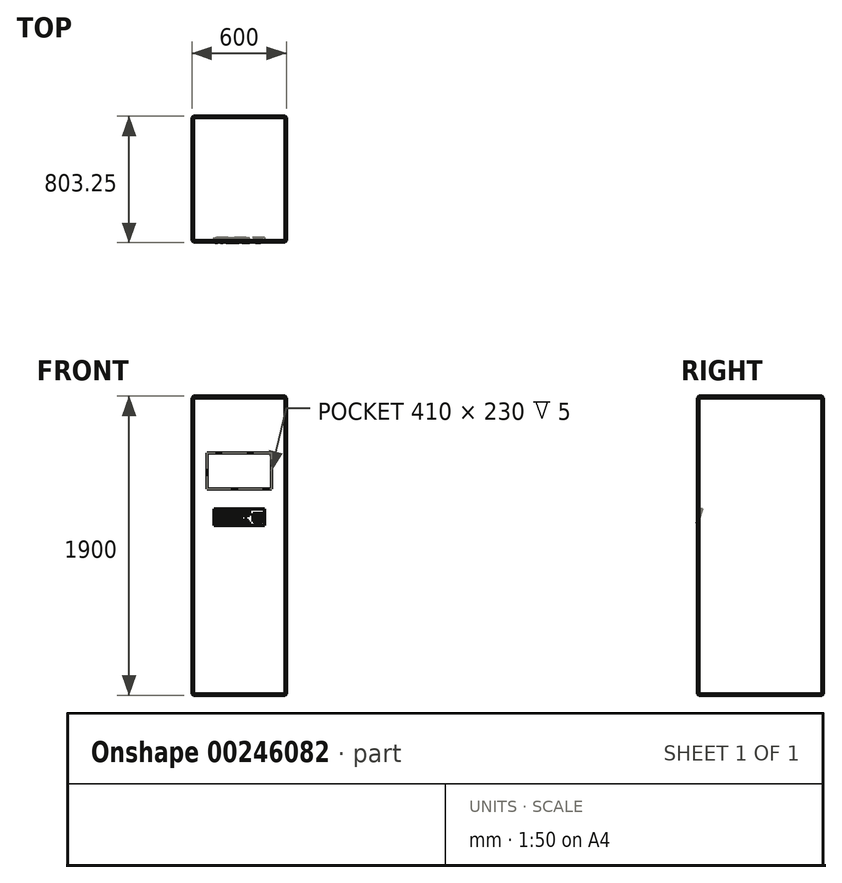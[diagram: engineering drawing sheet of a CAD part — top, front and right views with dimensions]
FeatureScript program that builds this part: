
annotation { "Feature Type Name" : "Feature", "Feature Type Description" : "" }
export const myFeature = defineFeature(function(context is Context, id is Id, definition is map)
    precondition{}
    {
        {
            var Q0;
            Q0=qCreatedBy(makeId("Top.planeOp"),FACE);
            var sketch = newSketch(context, id + "F0", { "sketchPlane" : qUnion([Q0])});
            skLineSegment(sketch, "E0.bottom", {"start": v(-300, 400) * mm, "end": v(300, 400) * mm});
            skLineSegment(sketch, "E0.top", {"start": v(-300, -400) * mm, "end": v(300, -400) * mm});
            skLineSegment(sketch, "E0.left", {"start": v(-300, 400) * mm, "end": v(-300, -400) * mm});
            skLineSegment(sketch, "E0.right", {"start": v(300, 400) * mm, "end": v(300, -400) * mm});
            skSolve(sketch);
        }
        {
            var Q0;
            Q0=makeQuery(id+"F0.imprint","IMPRINT",FACE,{"disambiguationData":[TD([[makeQuery(id+"F0.imprint","IMPRINT",EDGE,{"derivedFrom":sQuery(id+"F0.wireOp",EDGE,"E0.bottom")}),-1.0]])]});
            extrude(context, id + "F1", {"entities" : qUnion([Q0]), "depth" : 1900 * mm});
        }
        {
            var Q0;
            Q0=makeQuery(id+"F1.opExtrude","CAP_EDGE",EDGE,{"disambiguationData":[OSD([sQuery(id+"F0.wireOp",EDGE,"E0.top")])],"isStart":false});
            var Q1;
            Q1=makeQuery(id+"F1.opExtrude","SWEPT_EDGE",EDGE,{"disambiguationData":[OSD([sQuery(id+"F0.wireOp",EDGE,"E0.top"),sQuery(id+"F0.wireOp",EDGE,"E0.right")])]});
            var Q2;
            Q2=makeQuery(id+"F1.opExtrude","SWEPT_EDGE",EDGE,{"disambiguationData":[OSD([sQuery(id+"F0.wireOp",EDGE,"E0.top"),sQuery(id+"F0.wireOp",EDGE,"E0.left")])]});
            var Q3;
            Q3=makeQuery(id+"F1.opExtrude","CAP_EDGE",EDGE,{"disambiguationData":[OSD([sQuery(id+"F0.wireOp",EDGE,"E0.top")])],"isStart":true});
            var Q4;
            Q4=makeQuery(id+"F1.opExtrude","CAP_EDGE",EDGE,{"disambiguationData":[OSD([sQuery(id+"F0.wireOp",EDGE,"E0.right")])],"isStart":true});
            var Q5;
            Q5=makeQuery(id+"F1.opExtrude","CAP_EDGE",EDGE,{"disambiguationData":[OSD([sQuery(id+"F0.wireOp",EDGE,"E0.right")])],"isStart":false});
            var Q6;
            Q6=makeQuery(id+"F1.opExtrude","CAP_EDGE",EDGE,{"disambiguationData":[OSD([sQuery(id+"F0.wireOp",EDGE,"E0.left")])],"isStart":false});
            var Q7;
            Q7=makeQuery(id+"F1.opExtrude","CAP_EDGE",EDGE,{"disambiguationData":[OSD([sQuery(id+"F0.wireOp",EDGE,"E0.bottom")])],"isStart":false});
            var Q8;
            Q8=makeQuery(id+"F1.opExtrude","SWEPT_EDGE",EDGE,{"disambiguationData":[OSD([sQuery(id+"F0.wireOp",EDGE,"E0.bottom"),sQuery(id+"F0.wireOp",EDGE,"E0.right")])]});
            var Q9;
            Q9=makeQuery(id+"F1.opExtrude","SWEPT_EDGE",EDGE,{"disambiguationData":[OSD([sQuery(id+"F0.wireOp",EDGE,"E0.bottom"),sQuery(id+"F0.wireOp",EDGE,"E0.left")])]});
            var Q10;
            Q10=makeQuery(id+"F1.opExtrude","CAP_EDGE",EDGE,{"disambiguationData":[OSD([sQuery(id+"F0.wireOp",EDGE,"E0.bottom")])],"isStart":true});
            var Q11;
            Q11=makeQuery(id+"F1.opExtrude","CAP_EDGE",EDGE,{"disambiguationData":[OSD([sQuery(id+"F0.wireOp",EDGE,"E0.left")])],"isStart":true});
            chamfer(context, id + "F2", {"entities" : qUnion([Q0, Q1, Q2, Q3, Q4, Q5, Q6, Q7, Q8, Q9, Q10, Q11]), "width" : 10 * mm, "tangentPropagation" : true});
        }
        {
            var Q0;
            Q0=makeQuery(id+"F1.opExtrude","SWEPT_FACE",FACE,{"disambiguationData":[OSD([sQuery(id+"F0.wireOp",EDGE,"E0.top")])]});
            var sketch = newSketch(context, id + "F3", { "sketchPlane" : qUnion([Q0])});
            skLineSegment(sketch, "E1.bottom", {"start": v(205, 1540) * mm, "end": v(-205, 1540) * mm});
            skLineSegment(sketch, "E1.top", {"start": v(205, 1310) * mm, "end": v(-205, 1310) * mm});
            skLineSegment(sketch, "E1.left", {"start": v(205, 1540) * mm, "end": v(205, 1310) * mm});
            skLineSegment(sketch, "E1.right", {"start": v(-205, 1540) * mm, "end": v(-205, 1310) * mm});
            skPoint(sketch, "E1.middle", {"position": v(0, 1425) * mm});
            skSolve(sketch);
        }
        {
            var Q0;
            Q0=makeQuery(id+"F3.imprint","IMPRINT",FACE,{"disambiguationData":[TD([[makeQuery(id+"F3.imprint","IMPRINT",EDGE,{"derivedFrom":sQuery(id+"F3.wireOp",EDGE,"E1.bottom")}),1.0]])]});
            extrude(context, id + "F4", {"entities" : qUnion([Q0]), "operationType" : NewBodyOperationType.REMOVE, "oppositeDirection" : true, "depth" : 5 * mm});
        }
        {
            var Q0;
            Q0=makeQuery(id+"F1.opExtrude","SWEPT_FACE",FACE,{"disambiguationData":[OSD([sQuery(id+"F0.wireOp",EDGE,"E0.top")])]});
            var sketch = newSketch(context, id + "F5", { "sketchPlane" : qUnion([Q0])});
            skLineSegment(sketch, "E2.bottom", {"start": v(159.9, 1185) * mm, "end": v(-159.9, 1185) * mm});
            skLineSegment(sketch, "E2.top", {"start": v(159.9, 1080.2) * mm, "end": v(-159.9, 1080.2) * mm});
            skLineSegment(sketch, "E2.left", {"start": v(159.9, 1185) * mm, "end": v(159.9, 1080.2) * mm});
            skLineSegment(sketch, "E2.right", {"start": v(-159.9, 1185) * mm, "end": v(-159.9, 1080.2) * mm});
            skPoint(sketch, "E2.middle", {"position": v(0, 1132.6) * mm});
            skSolve(sketch);
        }
        {
            var Q0;
            Q0=makeQuery(id+"F5.imprint","IMPRINT",FACE,{"disambiguationData":[TD([[makeQuery(id+"F5.imprint","IMPRINT",EDGE,{"derivedFrom":sQuery(id+"F5.wireOp",EDGE,"E2.bottom")}),1.0]])]});
            extrude(context, id + "F6", {"entities" : qUnion([Q0]), "operationType" : NewBodyOperationType.REMOVE, "oppositeDirection" : true, "depth" : 30 * mm});
        }
        {
            var Q0;
            Q0=makeQuery(id+"F6.boolean.opBoolean","COPY",FACE,{"derivedFrom":makeQuery(id+"F6.opExtrude","SWEPT_FACE",FACE,{"disambiguationData":[OSD([sQuery(id+"F5.wireOp",EDGE,"E2.right")])]})});
            var sketch = newSketch(context, id + "F7", { "sketchPlane" : qUnion([Q0])});
            skLineSegment(sketch, "E3", {"start": v(-400, 1080.2) * mm, "end": v(-370, 1185) * mm});
            skLineSegment(sketch, "E4", {"start": v(-370, 1185) * mm, "end": v(-370, 1080.2) * mm});
            skLineSegment(sketch, "E5", {"start": v(-370, 1080.2) * mm, "end": v(-400, 1080.2) * mm});
            skSolve(sketch);
        }
        {
            var Q0;
            Q0=makeQuery(id+"F7.imprint","IMPRINT",FACE,{"disambiguationData":[TD([[makeQuery(id+"F7.imprint","IMPRINT",EDGE,{"derivedFrom":sQuery(id+"F7.wireOp",EDGE,"E3")}),-1.0]])]});
            extrude(context, id + "F8", {"entities" : qUnion([Q0]), "operationType" : NewBodyOperationType.ADD, "endBound" : BoundingType.UP_TO_NEXT, "depth" : 25 * mm});
        }
        {
            var Q0;
            Q0=makeQuery(id+"F8.opExtrude","SWEPT_FACE",FACE,{"disambiguationData":[OSD([sQuery(id+"F7.wireOp",EDGE,"E3")])]});
            var sketch = newSketch(context, id + "F9", { "sketchPlane" : qUnion([Q0])});
            skLineSegment(sketch, "E6.bottom", {"start": v(-137.9, 1010.42) * mm, "end": v(-151.9, 1010.42) * mm});
            skLineSegment(sketch, "E6.top", {"start": v(-137.9, 1024.42) * mm, "end": v(-151.9, 1024.42) * mm});
            skLineSegment(sketch, "E6.left", {"start": v(-137.9, 1010.42) * mm, "end": v(-137.9, 1024.42) * mm});
            skLineSegment(sketch, "E6.right", {"start": v(-151.9, 1010.42) * mm, "end": v(-151.9, 1024.42) * mm});
            skPoint(sketch, "E6.middle", {"position": v(-144.9, 1017.42) * mm});
            skLineSegment(sketch, "E7.0.1.0", {"start": v(-151.9, 991.91) * mm, "end": v(-151.9, 1005.91) * mm});
            skPoint(sketch, "E7.0.1.1", {"position": v(-144.9, 998.91) * mm});
            skLineSegment(sketch, "E7.0.1.2", {"start": v(-137.9, 991.91) * mm, "end": v(-151.9, 991.91) * mm});
            skLineSegment(sketch, "E7.0.1.3", {"start": v(-137.9, 1005.91) * mm, "end": v(-151.9, 1005.91) * mm});
            skLineSegment(sketch, "E7.0.1.4", {"start": v(-137.9, 991.91) * mm, "end": v(-137.9, 1005.91) * mm});
            skLineSegment(sketch, "E7.1.0.0", {"start": v(-134.85, 1010.42) * mm, "end": v(-134.85, 1024.42) * mm});
            skPoint(sketch, "E7.1.0.1", {"position": v(-127.85, 1017.42) * mm});
            skLineSegment(sketch, "E7.1.0.2", {"start": v(-120.85, 1010.42) * mm, "end": v(-134.85, 1010.42) * mm});
            skLineSegment(sketch, "E7.1.0.3", {"start": v(-120.85, 1024.42) * mm, "end": v(-134.85, 1024.42) * mm});
            skLineSegment(sketch, "E7.1.0.4", {"start": v(-120.85, 1010.42) * mm, "end": v(-120.85, 1024.42) * mm});
            skLineSegment(sketch, "E7.1.1.0", {"start": v(-134.85, 991.91) * mm, "end": v(-134.85, 1005.91) * mm});
            skPoint(sketch, "E7.1.1.1", {"position": v(-127.85, 998.91) * mm});
            skLineSegment(sketch, "E7.1.1.2", {"start": v(-120.85, 991.91) * mm, "end": v(-134.85, 991.91) * mm});
            skLineSegment(sketch, "E7.1.1.3", {"start": v(-120.85, 1005.91) * mm, "end": v(-134.85, 1005.91) * mm});
            skLineSegment(sketch, "E7.1.1.4", {"start": v(-120.85, 991.91) * mm, "end": v(-120.85, 1005.91) * mm});
            skLineSegment(sketch, "E7.2.0.0", {"start": v(-117.8, 1010.42) * mm, "end": v(-117.8, 1024.42) * mm});
            skPoint(sketch, "E7.2.0.1", {"position": v(-110.8, 1017.42) * mm});
            skLineSegment(sketch, "E7.2.0.2", {"start": v(-103.8, 1010.42) * mm, "end": v(-117.8, 1010.42) * mm});
            skLineSegment(sketch, "E7.2.0.3", {"start": v(-103.8, 1024.42) * mm, "end": v(-117.8, 1024.42) * mm});
            skLineSegment(sketch, "E7.2.0.4", {"start": v(-103.8, 1010.42) * mm, "end": v(-103.8, 1024.42) * mm});
            skLineSegment(sketch, "E7.2.1.0", {"start": v(-117.8, 991.91) * mm, "end": v(-117.8, 1005.91) * mm});
            skPoint(sketch, "E7.2.1.1", {"position": v(-110.8, 998.91) * mm});
            skLineSegment(sketch, "E7.2.1.2", {"start": v(-103.8, 991.91) * mm, "end": v(-117.8, 991.91) * mm});
            skLineSegment(sketch, "E7.2.1.3", {"start": v(-103.8, 1005.91) * mm, "end": v(-117.8, 1005.91) * mm});
            skLineSegment(sketch, "E7.2.1.4", {"start": v(-103.8, 991.91) * mm, "end": v(-103.8, 1005.91) * mm});
            skLineSegment(sketch, "E7.direction1", {"start": v(-151.9, 1010.42) * mm, "end": v(-134.85, 1010.42) * mm, "construction": true});
            skLineSegment(sketch, "E7.direction2", {"start": v(-151.9, 1010.42) * mm, "end": v(-151.9, 991.91) * mm, "construction": true});
            skLineSegment(sketch, "E8.0.3.0", {"start": v(-100.76, 1010.42) * mm, "end": v(-100.76, 1024.42) * mm});
            skPoint(sketch, "E8.3.3.0", {"position": v(-93.76, 1017.42) * mm});
            skLineSegment(sketch, "E8.4.3.0", {"start": v(-86.76, 1010.42) * mm, "end": v(-100.76, 1010.42) * mm});
            skLineSegment(sketch, "E8.7.3.0", {"start": v(-86.76, 1024.42) * mm, "end": v(-100.76, 1024.42) * mm});
            skLineSegment(sketch, "E8.10.3.0", {"start": v(-86.76, 1010.42) * mm, "end": v(-86.76, 1024.42) * mm});
            skLineSegment(sketch, "E8.0.3.1", {"start": v(-100.76, 991.91) * mm, "end": v(-100.76, 1005.91) * mm});
            skPoint(sketch, "E8.3.3.1", {"position": v(-93.76, 998.91) * mm});
            skLineSegment(sketch, "E8.4.3.1", {"start": v(-86.76, 991.91) * mm, "end": v(-100.76, 991.91) * mm});
            skLineSegment(sketch, "E8.7.3.1", {"start": v(-86.76, 1005.91) * mm, "end": v(-100.76, 1005.91) * mm});
            skLineSegment(sketch, "E8.10.3.1", {"start": v(-86.76, 991.91) * mm, "end": v(-86.76, 1005.91) * mm});
            skLineSegment(sketch, "E8.0.4.0", {"start": v(-83.71, 1010.42) * mm, "end": v(-83.71, 1024.42) * mm});
            skPoint(sketch, "E8.3.4.0", {"position": v(-76.71, 1017.42) * mm});
            skLineSegment(sketch, "E8.4.4.0", {"start": v(-69.71, 1010.42) * mm, "end": v(-83.71, 1010.42) * mm});
            skLineSegment(sketch, "E8.7.4.0", {"start": v(-69.71, 1024.42) * mm, "end": v(-83.71, 1024.42) * mm});
            skLineSegment(sketch, "E8.10.4.0", {"start": v(-69.71, 1010.42) * mm, "end": v(-69.71, 1024.42) * mm});
            skLineSegment(sketch, "E8.0.4.1", {"start": v(-83.71, 991.91) * mm, "end": v(-83.71, 1005.91) * mm});
            skPoint(sketch, "E8.3.4.1", {"position": v(-76.71, 998.91) * mm});
            skLineSegment(sketch, "E8.4.4.1", {"start": v(-69.71, 991.91) * mm, "end": v(-83.71, 991.91) * mm});
            skLineSegment(sketch, "E8.7.4.1", {"start": v(-69.71, 1005.91) * mm, "end": v(-83.71, 1005.91) * mm});
            skLineSegment(sketch, "E8.10.4.1", {"start": v(-69.71, 991.91) * mm, "end": v(-69.71, 1005.91) * mm});
            skLineSegment(sketch, "E8.0.5.0", {"start": v(-66.66, 1010.42) * mm, "end": v(-66.66, 1024.42) * mm});
            skPoint(sketch, "E8.3.5.0", {"position": v(-59.66, 1017.42) * mm});
            skLineSegment(sketch, "E8.4.5.0", {"start": v(-52.66, 1010.42) * mm, "end": v(-66.66, 1010.42) * mm});
            skLineSegment(sketch, "E8.7.5.0", {"start": v(-52.66, 1024.42) * mm, "end": v(-66.66, 1024.42) * mm});
            skLineSegment(sketch, "E8.10.5.0", {"start": v(-52.66, 1010.42) * mm, "end": v(-52.66, 1024.42) * mm});
            skLineSegment(sketch, "E8.0.5.1", {"start": v(-66.66, 991.91) * mm, "end": v(-66.66, 1005.91) * mm});
            skPoint(sketch, "E8.3.5.1", {"position": v(-59.66, 998.91) * mm});
            skLineSegment(sketch, "E8.4.5.1", {"start": v(-52.66, 991.91) * mm, "end": v(-66.66, 991.91) * mm});
            skLineSegment(sketch, "E8.7.5.1", {"start": v(-52.66, 1005.91) * mm, "end": v(-66.66, 1005.91) * mm});
            skLineSegment(sketch, "E8.10.5.1", {"start": v(-52.66, 991.91) * mm, "end": v(-52.66, 1005.91) * mm});
            skLineSegment(sketch, "E8.0.6.0", {"start": v(-49.62, 1010.42) * mm, "end": v(-49.62, 1024.42) * mm});
            skPoint(sketch, "E8.3.6.0", {"position": v(-42.62, 1017.42) * mm});
            skLineSegment(sketch, "E8.4.6.0", {"start": v(-35.62, 1010.42) * mm, "end": v(-49.62, 1010.42) * mm});
            skLineSegment(sketch, "E8.7.6.0", {"start": v(-35.62, 1024.42) * mm, "end": v(-49.62, 1024.42) * mm});
            skLineSegment(sketch, "E8.10.6.0", {"start": v(-35.62, 1010.42) * mm, "end": v(-35.62, 1024.42) * mm});
            skLineSegment(sketch, "E8.0.6.1", {"start": v(-49.62, 991.91) * mm, "end": v(-49.62, 1005.91) * mm});
            skPoint(sketch, "E8.3.6.1", {"position": v(-42.62, 998.91) * mm});
            skLineSegment(sketch, "E8.4.6.1", {"start": v(-35.62, 991.91) * mm, "end": v(-49.62, 991.91) * mm});
            skLineSegment(sketch, "E8.7.6.1", {"start": v(-35.62, 1005.91) * mm, "end": v(-49.62, 1005.91) * mm});
            skLineSegment(sketch, "E8.10.6.1", {"start": v(-35.62, 991.91) * mm, "end": v(-35.62, 1005.91) * mm});
            skLineSegment(sketch, "E8.0.7.0", {"start": v(-32.57, 1010.42) * mm, "end": v(-32.57, 1024.42) * mm});
            skPoint(sketch, "E8.3.7.0", {"position": v(-25.57, 1017.42) * mm});
            skLineSegment(sketch, "E8.4.7.0", {"start": v(-18.57, 1010.42) * mm, "end": v(-32.57, 1010.42) * mm});
            skLineSegment(sketch, "E8.7.7.0", {"start": v(-18.57, 1024.42) * mm, "end": v(-32.57, 1024.42) * mm});
            skLineSegment(sketch, "E8.10.7.0", {"start": v(-18.57, 1010.42) * mm, "end": v(-18.57, 1024.42) * mm});
            skLineSegment(sketch, "E8.0.7.1", {"start": v(-32.57, 991.91) * mm, "end": v(-32.57, 1005.91) * mm});
            skPoint(sketch, "E8.3.7.1", {"position": v(-25.57, 998.91) * mm});
            skLineSegment(sketch, "E8.4.7.1", {"start": v(-18.57, 991.91) * mm, "end": v(-32.57, 991.91) * mm});
            skLineSegment(sketch, "E8.7.7.1", {"start": v(-18.57, 1005.91) * mm, "end": v(-32.57, 1005.91) * mm});
            skLineSegment(sketch, "E8.10.7.1", {"start": v(-18.57, 991.91) * mm, "end": v(-18.57, 1005.91) * mm});
            skLineSegment(sketch, "E8.0.8.0", {"start": v(-15.52, 1010.42) * mm, "end": v(-15.52, 1024.42) * mm});
            skPoint(sketch, "E8.3.8.0", {"position": v(-8.52, 1017.42) * mm});
            skLineSegment(sketch, "E8.4.8.0", {"start": v(-1.52, 1010.42) * mm, "end": v(-15.52, 1010.42) * mm});
            skLineSegment(sketch, "E8.7.8.0", {"start": v(-1.52, 1024.42) * mm, "end": v(-15.52, 1024.42) * mm});
            skLineSegment(sketch, "E8.10.8.0", {"start": v(-1.52, 1010.42) * mm, "end": v(-1.52, 1024.42) * mm});
            skLineSegment(sketch, "E8.0.8.1", {"start": v(-15.52, 991.91) * mm, "end": v(-15.52, 1005.91) * mm});
            skPoint(sketch, "E8.3.8.1", {"position": v(-8.52, 998.91) * mm});
            skLineSegment(sketch, "E8.4.8.1", {"start": v(-1.52, 991.91) * mm, "end": v(-15.52, 991.91) * mm});
            skLineSegment(sketch, "E8.7.8.1", {"start": v(-1.52, 1005.91) * mm, "end": v(-15.52, 1005.91) * mm});
            skLineSegment(sketch, "E8.10.8.1", {"start": v(-1.52, 991.91) * mm, "end": v(-1.52, 1005.91) * mm});
            skLineSegment(sketch, "E8.0.9.0", {"start": v(1.52, 1010.42) * mm, "end": v(1.52, 1024.42) * mm});
            skPoint(sketch, "E8.3.9.0", {"position": v(8.52, 1017.42) * mm});
            skLineSegment(sketch, "E8.4.9.0", {"start": v(15.52, 1010.42) * mm, "end": v(1.52, 1010.42) * mm});
            skLineSegment(sketch, "E8.7.9.0", {"start": v(15.52, 1024.42) * mm, "end": v(1.52, 1024.42) * mm});
            skLineSegment(sketch, "E8.10.9.0", {"start": v(15.52, 1010.42) * mm, "end": v(15.52, 1024.42) * mm});
            skLineSegment(sketch, "E8.0.9.1", {"start": v(1.52, 991.91) * mm, "end": v(1.52, 1005.91) * mm});
            skPoint(sketch, "E8.3.9.1", {"position": v(8.52, 998.91) * mm});
            skLineSegment(sketch, "E8.4.9.1", {"start": v(15.52, 991.91) * mm, "end": v(1.52, 991.91) * mm});
            skLineSegment(sketch, "E8.7.9.1", {"start": v(15.52, 1005.91) * mm, "end": v(1.52, 1005.91) * mm});
            skLineSegment(sketch, "E8.10.9.1", {"start": v(15.52, 991.91) * mm, "end": v(15.52, 1005.91) * mm});
            skLineSegment(sketch, "E8.0.10.0", {"start": v(18.57, 1010.42) * mm, "end": v(18.57, 1024.42) * mm});
            skPoint(sketch, "E8.3.10.0", {"position": v(25.57, 1017.42) * mm});
            skLineSegment(sketch, "E8.4.10.0", {"start": v(32.57, 1010.42) * mm, "end": v(18.57, 1010.42) * mm});
            skLineSegment(sketch, "E8.7.10.0", {"start": v(32.57, 1024.42) * mm, "end": v(18.57, 1024.42) * mm});
            skLineSegment(sketch, "E8.10.10.0", {"start": v(32.57, 1010.42) * mm, "end": v(32.57, 1024.42) * mm});
            skLineSegment(sketch, "E8.0.10.1", {"start": v(18.57, 991.91) * mm, "end": v(18.57, 1005.91) * mm});
            skPoint(sketch, "E8.3.10.1", {"position": v(25.57, 998.91) * mm});
            skLineSegment(sketch, "E8.4.10.1", {"start": v(32.57, 991.91) * mm, "end": v(18.57, 991.91) * mm});
            skLineSegment(sketch, "E8.7.10.1", {"start": v(32.57, 1005.91) * mm, "end": v(18.57, 1005.91) * mm});
            skLineSegment(sketch, "E8.10.10.1", {"start": v(32.57, 991.91) * mm, "end": v(32.57, 1005.91) * mm});
            skLineSegment(sketch, "E8.0.11.0", {"start": v(35.62, 1010.42) * mm, "end": v(35.62, 1024.42) * mm});
            skPoint(sketch, "E8.3.11.0", {"position": v(42.62, 1017.42) * mm});
            skLineSegment(sketch, "E8.4.11.0", {"start": v(49.62, 1010.42) * mm, "end": v(35.62, 1010.42) * mm});
            skLineSegment(sketch, "E8.7.11.0", {"start": v(49.62, 1024.42) * mm, "end": v(35.62, 1024.42) * mm});
            skLineSegment(sketch, "E8.10.11.0", {"start": v(49.62, 1010.42) * mm, "end": v(49.62, 1024.42) * mm});
            skLineSegment(sketch, "E8.0.11.1", {"start": v(35.62, 991.91) * mm, "end": v(35.62, 1005.91) * mm});
            skPoint(sketch, "E8.3.11.1", {"position": v(42.62, 998.91) * mm});
            skLineSegment(sketch, "E8.4.11.1", {"start": v(49.62, 991.91) * mm, "end": v(35.62, 991.91) * mm});
            skLineSegment(sketch, "E8.7.11.1", {"start": v(49.62, 1005.91) * mm, "end": v(35.62, 1005.91) * mm});
            skLineSegment(sketch, "E8.10.11.1", {"start": v(49.62, 991.91) * mm, "end": v(49.62, 1005.91) * mm});
            skLineSegment(sketch, "E8.0.12.0", {"start": v(52.66, 1010.42) * mm, "end": v(52.66, 1024.42) * mm});
            skPoint(sketch, "E8.3.12.0", {"position": v(59.66, 1017.42) * mm});
            skLineSegment(sketch, "E8.4.12.0", {"start": v(66.66, 1010.42) * mm, "end": v(52.66, 1010.42) * mm});
            skLineSegment(sketch, "E8.7.12.0", {"start": v(66.66, 1024.42) * mm, "end": v(52.66, 1024.42) * mm});
            skLineSegment(sketch, "E8.10.12.0", {"start": v(66.66, 1010.42) * mm, "end": v(66.66, 1024.42) * mm});
            skLineSegment(sketch, "E8.0.12.1", {"start": v(52.66, 991.91) * mm, "end": v(52.66, 1005.91) * mm});
            skPoint(sketch, "E8.3.12.1", {"position": v(59.66, 998.91) * mm});
            skLineSegment(sketch, "E8.4.12.1", {"start": v(66.66, 991.91) * mm, "end": v(52.66, 991.91) * mm});
            skLineSegment(sketch, "E8.7.12.1", {"start": v(66.66, 1005.91) * mm, "end": v(52.66, 1005.91) * mm});
            skLineSegment(sketch, "E8.10.12.1", {"start": v(66.66, 991.91) * mm, "end": v(66.66, 1005.91) * mm});
            skLineSegment(sketch, "E8.0.13.0", {"start": v(69.71, 1010.42) * mm, "end": v(69.71, 1024.42) * mm});
            skPoint(sketch, "E8.3.13.0", {"position": v(76.71, 1017.42) * mm});
            skLineSegment(sketch, "E8.4.13.0", {"start": v(83.71, 1010.42) * mm, "end": v(69.71, 1010.42) * mm});
            skLineSegment(sketch, "E8.7.13.0", {"start": v(83.71, 1024.42) * mm, "end": v(69.71, 1024.42) * mm});
            skLineSegment(sketch, "E8.10.13.0", {"start": v(83.71, 1010.42) * mm, "end": v(83.71, 1024.42) * mm});
            skLineSegment(sketch, "E8.0.13.1", {"start": v(69.71, 991.91) * mm, "end": v(69.71, 1005.91) * mm});
            skPoint(sketch, "E8.3.13.1", {"position": v(76.71, 998.91) * mm});
            skLineSegment(sketch, "E8.4.13.1", {"start": v(83.71, 991.91) * mm, "end": v(69.71, 991.91) * mm});
            skLineSegment(sketch, "E8.7.13.1", {"start": v(83.71, 1005.91) * mm, "end": v(69.71, 1005.91) * mm});
            skLineSegment(sketch, "E8.10.13.1", {"start": v(83.71, 991.91) * mm, "end": v(83.71, 1005.91) * mm});
            skLineSegment(sketch, "E8.0.14.0", {"start": v(86.76, 1010.42) * mm, "end": v(86.76, 1024.42) * mm});
            skPoint(sketch, "E8.3.14.0", {"position": v(93.76, 1017.42) * mm});
            skLineSegment(sketch, "E8.4.14.0", {"start": v(100.76, 1010.42) * mm, "end": v(86.76, 1010.42) * mm});
            skLineSegment(sketch, "E8.7.14.0", {"start": v(100.76, 1024.42) * mm, "end": v(86.76, 1024.42) * mm});
            skLineSegment(sketch, "E8.10.14.0", {"start": v(100.76, 1010.42) * mm, "end": v(100.76, 1024.42) * mm});
            skLineSegment(sketch, "E8.0.14.1", {"start": v(86.76, 991.91) * mm, "end": v(86.76, 1005.91) * mm});
            skPoint(sketch, "E8.3.14.1", {"position": v(93.76, 998.91) * mm});
            skLineSegment(sketch, "E8.4.14.1", {"start": v(100.76, 991.91) * mm, "end": v(86.76, 991.91) * mm});
            skLineSegment(sketch, "E8.7.14.1", {"start": v(100.76, 1005.91) * mm, "end": v(86.76, 1005.91) * mm});
            skLineSegment(sketch, "E8.10.14.1", {"start": v(100.76, 991.91) * mm, "end": v(100.76, 1005.91) * mm});
            skLineSegment(sketch, "E8.0.15.0", {"start": v(103.8, 1010.42) * mm, "end": v(103.8, 1024.42) * mm});
            skPoint(sketch, "E8.3.15.0", {"position": v(110.8, 1017.42) * mm});
            skLineSegment(sketch, "E8.4.15.0", {"start": v(117.8, 1010.42) * mm, "end": v(103.8, 1010.42) * mm});
            skLineSegment(sketch, "E8.7.15.0", {"start": v(117.8, 1024.42) * mm, "end": v(103.8, 1024.42) * mm});
            skLineSegment(sketch, "E8.10.15.0", {"start": v(117.8, 1010.42) * mm, "end": v(117.8, 1024.42) * mm});
            skLineSegment(sketch, "E8.0.15.1", {"start": v(103.8, 991.91) * mm, "end": v(103.8, 1005.91) * mm});
            skPoint(sketch, "E8.3.15.1", {"position": v(110.8, 998.91) * mm});
            skLineSegment(sketch, "E8.4.15.1", {"start": v(117.8, 991.91) * mm, "end": v(103.8, 991.91) * mm});
            skLineSegment(sketch, "E8.7.15.1", {"start": v(117.8, 1005.91) * mm, "end": v(103.8, 1005.91) * mm});
            skLineSegment(sketch, "E8.10.15.1", {"start": v(117.8, 991.91) * mm, "end": v(117.8, 1005.91) * mm});
            skLineSegment(sketch, "E8.0.16.0", {"start": v(120.85, 1010.42) * mm, "end": v(120.85, 1024.42) * mm});
            skPoint(sketch, "E8.3.16.0", {"position": v(127.85, 1017.42) * mm});
            skLineSegment(sketch, "E8.4.16.0", {"start": v(134.85, 1010.42) * mm, "end": v(120.85, 1010.42) * mm});
            skLineSegment(sketch, "E8.7.16.0", {"start": v(134.85, 1024.42) * mm, "end": v(120.85, 1024.42) * mm});
            skLineSegment(sketch, "E8.10.16.0", {"start": v(134.85, 1010.42) * mm, "end": v(134.85, 1024.42) * mm});
            skLineSegment(sketch, "E8.0.16.1", {"start": v(120.85, 991.91) * mm, "end": v(120.85, 1005.91) * mm});
            skPoint(sketch, "E8.3.16.1", {"position": v(127.85, 998.91) * mm});
            skLineSegment(sketch, "E8.4.16.1", {"start": v(134.85, 991.91) * mm, "end": v(120.85, 991.91) * mm});
            skLineSegment(sketch, "E8.7.16.1", {"start": v(134.85, 1005.91) * mm, "end": v(120.85, 1005.91) * mm});
            skLineSegment(sketch, "E8.10.16.1", {"start": v(134.85, 991.91) * mm, "end": v(134.85, 1005.91) * mm});
            skLineSegment(sketch, "E8.0.17.0", {"start": v(137.9, 1010.42) * mm, "end": v(137.9, 1024.42) * mm});
            skPoint(sketch, "E8.3.17.0", {"position": v(144.9, 1017.42) * mm});
            skLineSegment(sketch, "E8.4.17.0", {"start": v(151.9, 1010.42) * mm, "end": v(137.9, 1010.42) * mm});
            skLineSegment(sketch, "E8.7.17.0", {"start": v(151.9, 1024.42) * mm, "end": v(137.9, 1024.42) * mm});
            skLineSegment(sketch, "E8.10.17.0", {"start": v(151.9, 1010.42) * mm, "end": v(151.9, 1024.42) * mm});
            skLineSegment(sketch, "E8.0.17.1", {"start": v(137.9, 991.91) * mm, "end": v(137.9, 1005.91) * mm});
            skPoint(sketch, "E8.3.17.1", {"position": v(144.9, 998.91) * mm});
            skLineSegment(sketch, "E8.4.17.1", {"start": v(151.9, 991.91) * mm, "end": v(137.9, 991.91) * mm});
            skLineSegment(sketch, "E8.7.17.1", {"start": v(151.9, 1005.91) * mm, "end": v(137.9, 1005.91) * mm});
            skLineSegment(sketch, "E8.10.17.1", {"start": v(151.9, 991.91) * mm, "end": v(151.9, 1005.91) * mm});
            skLineSegment(sketch, "E9.0.0.2", {"start": v(-151.9, 973.41) * mm, "end": v(-151.9, 987.41) * mm});
            skPoint(sketch, "E9.3.0.2", {"position": v(-144.9, 980.41) * mm});
            skLineSegment(sketch, "E9.4.0.2", {"start": v(-137.9, 973.41) * mm, "end": v(-151.9, 973.41) * mm});
            skLineSegment(sketch, "E9.7.0.2", {"start": v(-137.9, 987.41) * mm, "end": v(-151.9, 987.41) * mm});
            skLineSegment(sketch, "E9.10.0.2", {"start": v(-137.9, 973.41) * mm, "end": v(-137.9, 987.41) * mm});
            skLineSegment(sketch, "E9.0.0.3", {"start": v(-151.9, 954.9) * mm, "end": v(-151.9, 968.9) * mm});
            skPoint(sketch, "E9.3.0.3", {"position": v(-144.9, 961.9) * mm});
            skLineSegment(sketch, "E9.4.0.3", {"start": v(-137.9, 954.9) * mm, "end": v(-151.9, 954.9) * mm});
            skLineSegment(sketch, "E9.7.0.3", {"start": v(-137.9, 968.9) * mm, "end": v(-151.9, 968.9) * mm});
            skLineSegment(sketch, "E9.10.0.3", {"start": v(-137.9, 954.9) * mm, "end": v(-137.9, 968.9) * mm});
            skLineSegment(sketch, "E9.0.0.4", {"start": v(-151.9, 936.4) * mm, "end": v(-151.9, 950.4) * mm});
            skPoint(sketch, "E9.3.0.4", {"position": v(-144.9, 943.4) * mm});
            skLineSegment(sketch, "E9.4.0.4", {"start": v(-137.9, 936.4) * mm, "end": v(-151.9, 936.4) * mm});
            skLineSegment(sketch, "E9.7.0.4", {"start": v(-137.9, 950.4) * mm, "end": v(-151.9, 950.4) * mm});
            skLineSegment(sketch, "E9.10.0.4", {"start": v(-137.9, 936.4) * mm, "end": v(-137.9, 950.4) * mm});
            skLineSegment(sketch, "E9.0.1.2", {"start": v(-134.85, 973.41) * mm, "end": v(-134.85, 987.41) * mm});
            skPoint(sketch, "E9.3.1.2", {"position": v(-127.85, 980.41) * mm});
            skLineSegment(sketch, "E9.4.1.2", {"start": v(-120.85, 973.41) * mm, "end": v(-134.85, 973.41) * mm});
            skLineSegment(sketch, "E9.7.1.2", {"start": v(-120.85, 987.41) * mm, "end": v(-134.85, 987.41) * mm});
            skLineSegment(sketch, "E9.10.1.2", {"start": v(-120.85, 973.41) * mm, "end": v(-120.85, 987.41) * mm});
            skLineSegment(sketch, "E9.0.1.3", {"start": v(-134.85, 954.9) * mm, "end": v(-134.85, 968.9) * mm});
            skPoint(sketch, "E9.3.1.3", {"position": v(-127.85, 961.9) * mm});
            skLineSegment(sketch, "E9.4.1.3", {"start": v(-120.85, 954.9) * mm, "end": v(-134.85, 954.9) * mm});
            skLineSegment(sketch, "E9.7.1.3", {"start": v(-120.85, 968.9) * mm, "end": v(-134.85, 968.9) * mm});
            skLineSegment(sketch, "E9.10.1.3", {"start": v(-120.85, 954.9) * mm, "end": v(-120.85, 968.9) * mm});
            skLineSegment(sketch, "E9.0.1.4", {"start": v(-134.85, 936.4) * mm, "end": v(-134.85, 950.4) * mm});
            skPoint(sketch, "E9.3.1.4", {"position": v(-127.85, 943.4) * mm});
            skLineSegment(sketch, "E9.4.1.4", {"start": v(-120.85, 936.4) * mm, "end": v(-134.85, 936.4) * mm});
            skLineSegment(sketch, "E9.7.1.4", {"start": v(-120.85, 950.4) * mm, "end": v(-134.85, 950.4) * mm});
            skLineSegment(sketch, "E9.10.1.4", {"start": v(-120.85, 936.4) * mm, "end": v(-120.85, 950.4) * mm});
            skLineSegment(sketch, "E9.0.2.2", {"start": v(-117.8, 973.41) * mm, "end": v(-117.8, 987.41) * mm});
            skPoint(sketch, "E9.3.2.2", {"position": v(-110.8, 980.41) * mm});
            skLineSegment(sketch, "E9.4.2.2", {"start": v(-103.8, 973.41) * mm, "end": v(-117.8, 973.41) * mm});
            skLineSegment(sketch, "E9.7.2.2", {"start": v(-103.8, 987.41) * mm, "end": v(-117.8, 987.41) * mm});
            skLineSegment(sketch, "E9.10.2.2", {"start": v(-103.8, 973.41) * mm, "end": v(-103.8, 987.41) * mm});
            skLineSegment(sketch, "E9.0.2.3", {"start": v(-117.8, 954.9) * mm, "end": v(-117.8, 968.9) * mm});
            skPoint(sketch, "E9.3.2.3", {"position": v(-110.8, 961.9) * mm});
            skLineSegment(sketch, "E9.4.2.3", {"start": v(-103.8, 954.9) * mm, "end": v(-117.8, 954.9) * mm});
            skLineSegment(sketch, "E9.7.2.3", {"start": v(-103.8, 968.9) * mm, "end": v(-117.8, 968.9) * mm});
            skLineSegment(sketch, "E9.10.2.3", {"start": v(-103.8, 954.9) * mm, "end": v(-103.8, 968.9) * mm});
            skLineSegment(sketch, "E9.0.2.4", {"start": v(-117.8, 936.4) * mm, "end": v(-117.8, 950.4) * mm});
            skPoint(sketch, "E9.3.2.4", {"position": v(-110.8, 943.4) * mm});
            skLineSegment(sketch, "E9.4.2.4", {"start": v(-103.8, 936.4) * mm, "end": v(-117.8, 936.4) * mm});
            skLineSegment(sketch, "E9.7.2.4", {"start": v(-103.8, 950.4) * mm, "end": v(-117.8, 950.4) * mm});
            skLineSegment(sketch, "E9.10.2.4", {"start": v(-103.8, 936.4) * mm, "end": v(-103.8, 950.4) * mm});
            skLineSegment(sketch, "E9.0.3.2", {"start": v(-100.76, 973.41) * mm, "end": v(-100.76, 987.41) * mm});
            skPoint(sketch, "E9.3.3.2", {"position": v(-93.76, 980.41) * mm});
            skLineSegment(sketch, "E9.4.3.2", {"start": v(-86.76, 973.41) * mm, "end": v(-100.76, 973.41) * mm});
            skLineSegment(sketch, "E9.7.3.2", {"start": v(-86.76, 987.41) * mm, "end": v(-100.76, 987.41) * mm});
            skLineSegment(sketch, "E9.10.3.2", {"start": v(-86.76, 973.41) * mm, "end": v(-86.76, 987.41) * mm});
            skLineSegment(sketch, "E9.0.3.3", {"start": v(-100.76, 954.9) * mm, "end": v(-100.76, 968.9) * mm});
            skPoint(sketch, "E9.3.3.3", {"position": v(-93.76, 961.9) * mm});
            skLineSegment(sketch, "E9.4.3.3", {"start": v(-86.76, 954.9) * mm, "end": v(-100.76, 954.9) * mm});
            skLineSegment(sketch, "E9.7.3.3", {"start": v(-86.76, 968.9) * mm, "end": v(-100.76, 968.9) * mm});
            skLineSegment(sketch, "E9.10.3.3", {"start": v(-86.76, 954.9) * mm, "end": v(-86.76, 968.9) * mm});
            skLineSegment(sketch, "E9.0.3.4", {"start": v(-100.76, 936.4) * mm, "end": v(-100.76, 950.4) * mm});
            skPoint(sketch, "E9.3.3.4", {"position": v(-93.76, 943.4) * mm});
            skLineSegment(sketch, "E9.4.3.4", {"start": v(-86.76, 936.4) * mm, "end": v(-100.76, 936.4) * mm});
            skLineSegment(sketch, "E9.7.3.4", {"start": v(-86.76, 950.4) * mm, "end": v(-100.76, 950.4) * mm});
            skLineSegment(sketch, "E9.10.3.4", {"start": v(-86.76, 936.4) * mm, "end": v(-86.76, 950.4) * mm});
            skLineSegment(sketch, "E9.0.4.2", {"start": v(-83.71, 973.41) * mm, "end": v(-83.71, 987.41) * mm});
            skPoint(sketch, "E9.3.4.2", {"position": v(-76.71, 980.41) * mm});
            skLineSegment(sketch, "E9.4.4.2", {"start": v(-69.71, 973.41) * mm, "end": v(-83.71, 973.41) * mm});
            skLineSegment(sketch, "E9.7.4.2", {"start": v(-69.71, 987.41) * mm, "end": v(-83.71, 987.41) * mm});
            skLineSegment(sketch, "E9.10.4.2", {"start": v(-69.71, 973.41) * mm, "end": v(-69.71, 987.41) * mm});
            skLineSegment(sketch, "E9.0.4.3", {"start": v(-83.71, 954.9) * mm, "end": v(-83.71, 968.9) * mm});
            skPoint(sketch, "E9.3.4.3", {"position": v(-76.71, 961.9) * mm});
            skLineSegment(sketch, "E9.4.4.3", {"start": v(-69.71, 954.9) * mm, "end": v(-83.71, 954.9) * mm});
            skLineSegment(sketch, "E9.7.4.3", {"start": v(-69.71, 968.9) * mm, "end": v(-83.71, 968.9) * mm});
            skLineSegment(sketch, "E9.10.4.3", {"start": v(-69.71, 954.9) * mm, "end": v(-69.71, 968.9) * mm});
            skLineSegment(sketch, "E9.0.4.4", {"start": v(-83.71, 936.4) * mm, "end": v(-83.71, 950.4) * mm});
            skPoint(sketch, "E9.3.4.4", {"position": v(-76.71, 943.4) * mm});
            skLineSegment(sketch, "E9.4.4.4", {"start": v(-69.71, 936.4) * mm, "end": v(-83.71, 936.4) * mm});
            skLineSegment(sketch, "E9.7.4.4", {"start": v(-69.71, 950.4) * mm, "end": v(-83.71, 950.4) * mm});
            skLineSegment(sketch, "E9.10.4.4", {"start": v(-69.71, 936.4) * mm, "end": v(-69.71, 950.4) * mm});
            skLineSegment(sketch, "E9.0.5.2", {"start": v(-66.66, 973.41) * mm, "end": v(-66.66, 987.41) * mm});
            skPoint(sketch, "E9.3.5.2", {"position": v(-59.66, 980.41) * mm});
            skLineSegment(sketch, "E9.4.5.2", {"start": v(-52.66, 973.41) * mm, "end": v(-66.66, 973.41) * mm});
            skLineSegment(sketch, "E9.7.5.2", {"start": v(-52.66, 987.41) * mm, "end": v(-66.66, 987.41) * mm});
            skLineSegment(sketch, "E9.10.5.2", {"start": v(-52.66, 973.41) * mm, "end": v(-52.66, 987.41) * mm});
            skLineSegment(sketch, "E9.0.5.3", {"start": v(-66.66, 954.9) * mm, "end": v(-66.66, 968.9) * mm});
            skPoint(sketch, "E9.3.5.3", {"position": v(-59.66, 961.9) * mm});
            skLineSegment(sketch, "E9.4.5.3", {"start": v(-52.66, 954.9) * mm, "end": v(-66.66, 954.9) * mm});
            skLineSegment(sketch, "E9.7.5.3", {"start": v(-52.66, 968.9) * mm, "end": v(-66.66, 968.9) * mm});
            skLineSegment(sketch, "E9.10.5.3", {"start": v(-52.66, 954.9) * mm, "end": v(-52.66, 968.9) * mm});
            skLineSegment(sketch, "E9.0.5.4", {"start": v(-66.66, 936.4) * mm, "end": v(-66.66, 950.4) * mm});
            skPoint(sketch, "E9.3.5.4", {"position": v(-59.66, 943.4) * mm});
            skLineSegment(sketch, "E9.4.5.4", {"start": v(-52.66, 936.4) * mm, "end": v(-66.66, 936.4) * mm});
            skLineSegment(sketch, "E9.7.5.4", {"start": v(-52.66, 950.4) * mm, "end": v(-66.66, 950.4) * mm});
            skLineSegment(sketch, "E9.10.5.4", {"start": v(-52.66, 936.4) * mm, "end": v(-52.66, 950.4) * mm});
            skLineSegment(sketch, "E9.0.6.2", {"start": v(-49.62, 973.41) * mm, "end": v(-49.62, 987.41) * mm});
            skPoint(sketch, "E9.3.6.2", {"position": v(-42.62, 980.41) * mm});
            skLineSegment(sketch, "E9.4.6.2", {"start": v(-35.62, 973.41) * mm, "end": v(-49.62, 973.41) * mm});
            skLineSegment(sketch, "E9.7.6.2", {"start": v(-35.62, 987.41) * mm, "end": v(-49.62, 987.41) * mm});
            skLineSegment(sketch, "E9.10.6.2", {"start": v(-35.62, 973.41) * mm, "end": v(-35.62, 987.41) * mm});
            skLineSegment(sketch, "E9.0.6.3", {"start": v(-49.62, 954.9) * mm, "end": v(-49.62, 968.9) * mm});
            skPoint(sketch, "E9.3.6.3", {"position": v(-42.62, 961.9) * mm});
            skLineSegment(sketch, "E9.4.6.3", {"start": v(-35.62, 954.9) * mm, "end": v(-49.62, 954.9) * mm});
            skLineSegment(sketch, "E9.7.6.3", {"start": v(-35.62, 968.9) * mm, "end": v(-49.62, 968.9) * mm});
            skLineSegment(sketch, "E9.10.6.3", {"start": v(-35.62, 954.9) * mm, "end": v(-35.62, 968.9) * mm});
            skLineSegment(sketch, "E9.0.6.4", {"start": v(-49.62, 936.4) * mm, "end": v(-49.62, 950.4) * mm});
            skPoint(sketch, "E9.3.6.4", {"position": v(-42.62, 943.4) * mm});
            skLineSegment(sketch, "E9.4.6.4", {"start": v(-35.62, 936.4) * mm, "end": v(-49.62, 936.4) * mm});
            skLineSegment(sketch, "E9.7.6.4", {"start": v(-35.62, 950.4) * mm, "end": v(-49.62, 950.4) * mm});
            skLineSegment(sketch, "E9.10.6.4", {"start": v(-35.62, 936.4) * mm, "end": v(-35.62, 950.4) * mm});
            skLineSegment(sketch, "E9.0.7.2", {"start": v(-32.57, 973.41) * mm, "end": v(-32.57, 987.41) * mm});
            skPoint(sketch, "E9.3.7.2", {"position": v(-25.57, 980.41) * mm});
            skLineSegment(sketch, "E9.4.7.2", {"start": v(-18.57, 973.41) * mm, "end": v(-32.57, 973.41) * mm});
            skLineSegment(sketch, "E9.7.7.2", {"start": v(-18.57, 987.41) * mm, "end": v(-32.57, 987.41) * mm});
            skLineSegment(sketch, "E9.10.7.2", {"start": v(-18.57, 973.41) * mm, "end": v(-18.57, 987.41) * mm});
            skLineSegment(sketch, "E9.0.7.3", {"start": v(-32.57, 954.9) * mm, "end": v(-32.57, 968.9) * mm});
            skPoint(sketch, "E9.3.7.3", {"position": v(-25.57, 961.9) * mm});
            skLineSegment(sketch, "E9.4.7.3", {"start": v(-18.57, 954.9) * mm, "end": v(-32.57, 954.9) * mm});
            skLineSegment(sketch, "E9.7.7.3", {"start": v(-18.57, 968.9) * mm, "end": v(-32.57, 968.9) * mm});
            skLineSegment(sketch, "E9.10.7.3", {"start": v(-18.57, 954.9) * mm, "end": v(-18.57, 968.9) * mm});
            skLineSegment(sketch, "E9.0.7.4", {"start": v(-32.57, 936.4) * mm, "end": v(-32.57, 950.4) * mm});
            skPoint(sketch, "E9.3.7.4", {"position": v(-25.57, 943.4) * mm});
            skLineSegment(sketch, "E9.4.7.4", {"start": v(-18.57, 936.4) * mm, "end": v(-32.57, 936.4) * mm});
            skLineSegment(sketch, "E9.7.7.4", {"start": v(-18.57, 950.4) * mm, "end": v(-32.57, 950.4) * mm});
            skLineSegment(sketch, "E9.10.7.4", {"start": v(-18.57, 936.4) * mm, "end": v(-18.57, 950.4) * mm});
            skLineSegment(sketch, "E9.0.8.2", {"start": v(-15.52, 973.41) * mm, "end": v(-15.52, 987.41) * mm});
            skPoint(sketch, "E9.3.8.2", {"position": v(-8.52, 980.41) * mm});
            skLineSegment(sketch, "E9.4.8.2", {"start": v(-1.52, 973.41) * mm, "end": v(-15.52, 973.41) * mm});
            skLineSegment(sketch, "E9.7.8.2", {"start": v(-1.52, 987.41) * mm, "end": v(-15.52, 987.41) * mm});
            skLineSegment(sketch, "E9.10.8.2", {"start": v(-1.52, 973.41) * mm, "end": v(-1.52, 987.41) * mm});
            skLineSegment(sketch, "E9.0.8.3", {"start": v(-15.52, 954.9) * mm, "end": v(-15.52, 968.9) * mm});
            skPoint(sketch, "E9.3.8.3", {"position": v(-8.52, 961.9) * mm});
            skLineSegment(sketch, "E9.4.8.3", {"start": v(-1.52, 954.9) * mm, "end": v(-15.52, 954.9) * mm});
            skLineSegment(sketch, "E9.7.8.3", {"start": v(-1.52, 968.9) * mm, "end": v(-15.52, 968.9) * mm});
            skLineSegment(sketch, "E9.10.8.3", {"start": v(-1.52, 954.9) * mm, "end": v(-1.52, 968.9) * mm});
            skLineSegment(sketch, "E9.0.8.4", {"start": v(-15.52, 936.4) * mm, "end": v(-15.52, 950.4) * mm});
            skPoint(sketch, "E9.3.8.4", {"position": v(-8.52, 943.4) * mm});
            skLineSegment(sketch, "E9.4.8.4", {"start": v(-1.52, 936.4) * mm, "end": v(-15.52, 936.4) * mm});
            skLineSegment(sketch, "E9.7.8.4", {"start": v(-1.52, 950.4) * mm, "end": v(-15.52, 950.4) * mm});
            skLineSegment(sketch, "E9.10.8.4", {"start": v(-1.52, 936.4) * mm, "end": v(-1.52, 950.4) * mm});
            skLineSegment(sketch, "E9.0.9.2", {"start": v(1.52, 973.41) * mm, "end": v(1.52, 987.41) * mm});
            skPoint(sketch, "E9.3.9.2", {"position": v(8.52, 980.41) * mm});
            skLineSegment(sketch, "E9.4.9.2", {"start": v(15.52, 973.41) * mm, "end": v(1.52, 973.41) * mm});
            skLineSegment(sketch, "E9.7.9.2", {"start": v(15.52, 987.41) * mm, "end": v(1.52, 987.41) * mm});
            skLineSegment(sketch, "E9.10.9.2", {"start": v(15.52, 973.41) * mm, "end": v(15.52, 987.41) * mm});
            skLineSegment(sketch, "E9.0.9.3", {"start": v(1.52, 954.9) * mm, "end": v(1.52, 968.9) * mm});
            skPoint(sketch, "E9.3.9.3", {"position": v(8.52, 961.9) * mm});
            skLineSegment(sketch, "E9.4.9.3", {"start": v(15.52, 954.9) * mm, "end": v(1.52, 954.9) * mm});
            skLineSegment(sketch, "E9.7.9.3", {"start": v(15.52, 968.9) * mm, "end": v(1.52, 968.9) * mm});
            skLineSegment(sketch, "E9.10.9.3", {"start": v(15.52, 954.9) * mm, "end": v(15.52, 968.9) * mm});
            skLineSegment(sketch, "E9.0.9.4", {"start": v(1.52, 936.4) * mm, "end": v(1.52, 950.4) * mm});
            skPoint(sketch, "E9.3.9.4", {"position": v(8.52, 943.4) * mm});
            skLineSegment(sketch, "E9.4.9.4", {"start": v(15.52, 936.4) * mm, "end": v(1.52, 936.4) * mm});
            skLineSegment(sketch, "E9.7.9.4", {"start": v(15.52, 950.4) * mm, "end": v(1.52, 950.4) * mm});
            skLineSegment(sketch, "E9.10.9.4", {"start": v(15.52, 936.4) * mm, "end": v(15.52, 950.4) * mm});
            skLineSegment(sketch, "E9.0.10.2", {"start": v(18.57, 973.41) * mm, "end": v(18.57, 987.41) * mm});
            skPoint(sketch, "E9.3.10.2", {"position": v(25.57, 980.41) * mm});
            skLineSegment(sketch, "E9.4.10.2", {"start": v(32.57, 973.41) * mm, "end": v(18.57, 973.41) * mm});
            skLineSegment(sketch, "E9.7.10.2", {"start": v(32.57, 987.41) * mm, "end": v(18.57, 987.41) * mm});
            skLineSegment(sketch, "E9.10.10.2", {"start": v(32.57, 973.41) * mm, "end": v(32.57, 987.41) * mm});
            skLineSegment(sketch, "E9.0.10.3", {"start": v(18.57, 954.9) * mm, "end": v(18.57, 968.9) * mm});
            skPoint(sketch, "E9.3.10.3", {"position": v(25.57, 961.9) * mm});
            skLineSegment(sketch, "E9.4.10.3", {"start": v(32.57, 954.9) * mm, "end": v(18.57, 954.9) * mm});
            skLineSegment(sketch, "E9.7.10.3", {"start": v(32.57, 968.9) * mm, "end": v(18.57, 968.9) * mm});
            skLineSegment(sketch, "E9.10.10.3", {"start": v(32.57, 954.9) * mm, "end": v(32.57, 968.9) * mm});
            skLineSegment(sketch, "E9.0.10.4", {"start": v(18.57, 936.4) * mm, "end": v(18.57, 950.4) * mm});
            skPoint(sketch, "E9.3.10.4", {"position": v(25.57, 943.4) * mm});
            skLineSegment(sketch, "E9.4.10.4", {"start": v(32.57, 936.4) * mm, "end": v(18.57, 936.4) * mm});
            skLineSegment(sketch, "E9.7.10.4", {"start": v(32.57, 950.4) * mm, "end": v(18.57, 950.4) * mm});
            skLineSegment(sketch, "E9.10.10.4", {"start": v(32.57, 936.4) * mm, "end": v(32.57, 950.4) * mm});
            skLineSegment(sketch, "E9.0.11.2", {"start": v(35.62, 973.41) * mm, "end": v(35.62, 987.41) * mm});
            skPoint(sketch, "E9.3.11.2", {"position": v(42.62, 980.41) * mm});
            skLineSegment(sketch, "E9.4.11.2", {"start": v(49.62, 973.41) * mm, "end": v(35.62, 973.41) * mm});
            skLineSegment(sketch, "E9.7.11.2", {"start": v(49.62, 987.41) * mm, "end": v(35.62, 987.41) * mm});
            skLineSegment(sketch, "E9.10.11.2", {"start": v(49.62, 973.41) * mm, "end": v(49.62, 987.41) * mm});
            skLineSegment(sketch, "E9.0.11.3", {"start": v(35.62, 954.9) * mm, "end": v(35.62, 968.9) * mm});
            skPoint(sketch, "E9.3.11.3", {"position": v(42.62, 961.9) * mm});
            skLineSegment(sketch, "E9.4.11.3", {"start": v(49.62, 954.9) * mm, "end": v(35.62, 954.9) * mm});
            skLineSegment(sketch, "E9.7.11.3", {"start": v(49.62, 968.9) * mm, "end": v(35.62, 968.9) * mm});
            skLineSegment(sketch, "E9.10.11.3", {"start": v(49.62, 954.9) * mm, "end": v(49.62, 968.9) * mm});
            skLineSegment(sketch, "E9.0.11.4", {"start": v(35.62, 936.4) * mm, "end": v(35.62, 950.4) * mm});
            skPoint(sketch, "E9.3.11.4", {"position": v(42.62, 943.4) * mm});
            skLineSegment(sketch, "E9.4.11.4", {"start": v(49.62, 936.4) * mm, "end": v(35.62, 936.4) * mm});
            skLineSegment(sketch, "E9.7.11.4", {"start": v(49.62, 950.4) * mm, "end": v(35.62, 950.4) * mm});
            skLineSegment(sketch, "E9.10.11.4", {"start": v(49.62, 936.4) * mm, "end": v(49.62, 950.4) * mm});
            skLineSegment(sketch, "E9.0.12.2", {"start": v(52.66, 973.41) * mm, "end": v(52.66, 987.41) * mm});
            skPoint(sketch, "E9.3.12.2", {"position": v(59.66, 980.41) * mm});
            skLineSegment(sketch, "E9.4.12.2", {"start": v(66.66, 973.41) * mm, "end": v(52.66, 973.41) * mm});
            skLineSegment(sketch, "E9.7.12.2", {"start": v(66.66, 987.41) * mm, "end": v(52.66, 987.41) * mm});
            skLineSegment(sketch, "E9.10.12.2", {"start": v(66.66, 973.41) * mm, "end": v(66.66, 987.41) * mm});
            skLineSegment(sketch, "E9.0.12.3", {"start": v(52.66, 954.9) * mm, "end": v(52.66, 968.9) * mm});
            skPoint(sketch, "E9.3.12.3", {"position": v(59.66, 961.9) * mm});
            skLineSegment(sketch, "E9.4.12.3", {"start": v(66.66, 954.9) * mm, "end": v(52.66, 954.9) * mm});
            skLineSegment(sketch, "E9.7.12.3", {"start": v(66.66, 968.9) * mm, "end": v(52.66, 968.9) * mm});
            skLineSegment(sketch, "E9.10.12.3", {"start": v(66.66, 954.9) * mm, "end": v(66.66, 968.9) * mm});
            skLineSegment(sketch, "E9.0.12.4", {"start": v(52.66, 936.4) * mm, "end": v(52.66, 950.4) * mm});
            skPoint(sketch, "E9.3.12.4", {"position": v(59.66, 943.4) * mm});
            skLineSegment(sketch, "E9.4.12.4", {"start": v(66.66, 936.4) * mm, "end": v(52.66, 936.4) * mm});
            skLineSegment(sketch, "E9.7.12.4", {"start": v(66.66, 950.4) * mm, "end": v(52.66, 950.4) * mm});
            skLineSegment(sketch, "E9.10.12.4", {"start": v(66.66, 936.4) * mm, "end": v(66.66, 950.4) * mm});
            skLineSegment(sketch, "E9.0.13.2", {"start": v(69.71, 973.41) * mm, "end": v(69.71, 987.41) * mm});
            skPoint(sketch, "E9.3.13.2", {"position": v(76.71, 980.41) * mm});
            skLineSegment(sketch, "E9.4.13.2", {"start": v(83.71, 973.41) * mm, "end": v(69.71, 973.41) * mm});
            skLineSegment(sketch, "E9.7.13.2", {"start": v(83.71, 987.41) * mm, "end": v(69.71, 987.41) * mm});
            skLineSegment(sketch, "E9.10.13.2", {"start": v(83.71, 973.41) * mm, "end": v(83.71, 987.41) * mm});
            skLineSegment(sketch, "E9.0.13.3", {"start": v(69.71, 954.9) * mm, "end": v(69.71, 968.9) * mm});
            skPoint(sketch, "E9.3.13.3", {"position": v(76.71, 961.9) * mm});
            skLineSegment(sketch, "E9.4.13.3", {"start": v(83.71, 954.9) * mm, "end": v(69.71, 954.9) * mm});
            skLineSegment(sketch, "E9.7.13.3", {"start": v(83.71, 968.9) * mm, "end": v(69.71, 968.9) * mm});
            skLineSegment(sketch, "E9.10.13.3", {"start": v(83.71, 954.9) * mm, "end": v(83.71, 968.9) * mm});
            skLineSegment(sketch, "E9.0.13.4", {"start": v(69.71, 936.4) * mm, "end": v(69.71, 950.4) * mm});
            skPoint(sketch, "E9.3.13.4", {"position": v(76.71, 943.4) * mm});
            skLineSegment(sketch, "E9.4.13.4", {"start": v(83.71, 936.4) * mm, "end": v(69.71, 936.4) * mm});
            skLineSegment(sketch, "E9.7.13.4", {"start": v(83.71, 950.4) * mm, "end": v(69.71, 950.4) * mm});
            skLineSegment(sketch, "E9.10.13.4", {"start": v(83.71, 936.4) * mm, "end": v(83.71, 950.4) * mm});
            skLineSegment(sketch, "E9.0.14.2", {"start": v(86.76, 973.41) * mm, "end": v(86.76, 987.41) * mm});
            skPoint(sketch, "E9.3.14.2", {"position": v(93.76, 980.41) * mm});
            skLineSegment(sketch, "E9.4.14.2", {"start": v(100.76, 973.41) * mm, "end": v(86.76, 973.41) * mm});
            skLineSegment(sketch, "E9.7.14.2", {"start": v(100.76, 987.41) * mm, "end": v(86.76, 987.41) * mm});
            skLineSegment(sketch, "E9.10.14.2", {"start": v(100.76, 973.41) * mm, "end": v(100.76, 987.41) * mm});
            skLineSegment(sketch, "E9.0.14.3", {"start": v(86.76, 954.9) * mm, "end": v(86.76, 968.9) * mm});
            skPoint(sketch, "E9.3.14.3", {"position": v(93.76, 961.9) * mm});
            skLineSegment(sketch, "E9.4.14.3", {"start": v(100.76, 954.9) * mm, "end": v(86.76, 954.9) * mm});
            skLineSegment(sketch, "E9.7.14.3", {"start": v(100.76, 968.9) * mm, "end": v(86.76, 968.9) * mm});
            skLineSegment(sketch, "E9.10.14.3", {"start": v(100.76, 954.9) * mm, "end": v(100.76, 968.9) * mm});
            skLineSegment(sketch, "E9.0.14.4", {"start": v(86.76, 936.4) * mm, "end": v(86.76, 950.4) * mm});
            skPoint(sketch, "E9.3.14.4", {"position": v(93.76, 943.4) * mm});
            skLineSegment(sketch, "E9.4.14.4", {"start": v(100.76, 936.4) * mm, "end": v(86.76, 936.4) * mm});
            skLineSegment(sketch, "E9.7.14.4", {"start": v(100.76, 950.4) * mm, "end": v(86.76, 950.4) * mm});
            skLineSegment(sketch, "E9.10.14.4", {"start": v(100.76, 936.4) * mm, "end": v(100.76, 950.4) * mm});
            skLineSegment(sketch, "E9.0.15.2", {"start": v(103.8, 973.41) * mm, "end": v(103.8, 987.41) * mm});
            skPoint(sketch, "E9.3.15.2", {"position": v(110.8, 980.41) * mm});
            skLineSegment(sketch, "E9.4.15.2", {"start": v(117.8, 973.41) * mm, "end": v(103.8, 973.41) * mm});
            skLineSegment(sketch, "E9.7.15.2", {"start": v(117.8, 987.41) * mm, "end": v(103.8, 987.41) * mm});
            skLineSegment(sketch, "E9.10.15.2", {"start": v(117.8, 973.41) * mm, "end": v(117.8, 987.41) * mm});
            skLineSegment(sketch, "E9.0.15.3", {"start": v(103.8, 954.9) * mm, "end": v(103.8, 968.9) * mm});
            skPoint(sketch, "E9.3.15.3", {"position": v(110.8, 961.9) * mm});
            skLineSegment(sketch, "E9.4.15.3", {"start": v(117.8, 954.9) * mm, "end": v(103.8, 954.9) * mm});
            skLineSegment(sketch, "E9.7.15.3", {"start": v(117.8, 968.9) * mm, "end": v(103.8, 968.9) * mm});
            skLineSegment(sketch, "E9.10.15.3", {"start": v(117.8, 954.9) * mm, "end": v(117.8, 968.9) * mm});
            skLineSegment(sketch, "E9.0.15.4", {"start": v(103.8, 936.4) * mm, "end": v(103.8, 950.4) * mm});
            skPoint(sketch, "E9.3.15.4", {"position": v(110.8, 943.4) * mm});
            skLineSegment(sketch, "E9.4.15.4", {"start": v(117.8, 936.4) * mm, "end": v(103.8, 936.4) * mm});
            skLineSegment(sketch, "E9.7.15.4", {"start": v(117.8, 950.4) * mm, "end": v(103.8, 950.4) * mm});
            skLineSegment(sketch, "E9.10.15.4", {"start": v(117.8, 936.4) * mm, "end": v(117.8, 950.4) * mm});
            skLineSegment(sketch, "E9.0.16.2", {"start": v(120.85, 973.41) * mm, "end": v(120.85, 987.41) * mm});
            skPoint(sketch, "E9.3.16.2", {"position": v(127.85, 980.41) * mm});
            skLineSegment(sketch, "E9.4.16.2", {"start": v(134.85, 973.41) * mm, "end": v(120.85, 973.41) * mm});
            skLineSegment(sketch, "E9.7.16.2", {"start": v(134.85, 987.41) * mm, "end": v(120.85, 987.41) * mm});
            skLineSegment(sketch, "E9.10.16.2", {"start": v(134.85, 973.41) * mm, "end": v(134.85, 987.41) * mm});
            skLineSegment(sketch, "E9.0.16.3", {"start": v(120.85, 954.9) * mm, "end": v(120.85, 968.9) * mm});
            skPoint(sketch, "E9.3.16.3", {"position": v(127.85, 961.9) * mm});
            skLineSegment(sketch, "E9.4.16.3", {"start": v(134.85, 954.9) * mm, "end": v(120.85, 954.9) * mm});
            skLineSegment(sketch, "E9.7.16.3", {"start": v(134.85, 968.9) * mm, "end": v(120.85, 968.9) * mm});
            skLineSegment(sketch, "E9.10.16.3", {"start": v(134.85, 954.9) * mm, "end": v(134.85, 968.9) * mm});
            skLineSegment(sketch, "E9.0.16.4", {"start": v(120.85, 936.4) * mm, "end": v(120.85, 950.4) * mm});
            skPoint(sketch, "E9.3.16.4", {"position": v(127.85, 943.4) * mm});
            skLineSegment(sketch, "E9.4.16.4", {"start": v(134.85, 936.4) * mm, "end": v(120.85, 936.4) * mm});
            skLineSegment(sketch, "E9.7.16.4", {"start": v(134.85, 950.4) * mm, "end": v(120.85, 950.4) * mm});
            skLineSegment(sketch, "E9.10.16.4", {"start": v(134.85, 936.4) * mm, "end": v(134.85, 950.4) * mm});
            skLineSegment(sketch, "E9.0.17.2", {"start": v(137.9, 973.41) * mm, "end": v(137.9, 987.41) * mm});
            skPoint(sketch, "E9.3.17.2", {"position": v(144.9, 980.41) * mm});
            skLineSegment(sketch, "E9.4.17.2", {"start": v(151.9, 973.41) * mm, "end": v(137.9, 973.41) * mm});
            skLineSegment(sketch, "E9.7.17.2", {"start": v(151.9, 987.41) * mm, "end": v(137.9, 987.41) * mm});
            skLineSegment(sketch, "E9.10.17.2", {"start": v(151.9, 973.41) * mm, "end": v(151.9, 987.41) * mm});
            skLineSegment(sketch, "E9.0.17.3", {"start": v(137.9, 954.9) * mm, "end": v(137.9, 968.9) * mm});
            skPoint(sketch, "E9.3.17.3", {"position": v(144.9, 961.9) * mm});
            skLineSegment(sketch, "E9.4.17.3", {"start": v(151.9, 954.9) * mm, "end": v(137.9, 954.9) * mm});
            skLineSegment(sketch, "E9.7.17.3", {"start": v(151.9, 968.9) * mm, "end": v(137.9, 968.9) * mm});
            skLineSegment(sketch, "E9.10.17.3", {"start": v(151.9, 954.9) * mm, "end": v(151.9, 968.9) * mm});
            skLineSegment(sketch, "E9.0.17.4", {"start": v(137.9, 936.4) * mm, "end": v(137.9, 950.4) * mm});
            skPoint(sketch, "E9.3.17.4", {"position": v(144.9, 943.4) * mm});
            skLineSegment(sketch, "E9.4.17.4", {"start": v(151.9, 936.4) * mm, "end": v(137.9, 936.4) * mm});
            skLineSegment(sketch, "E9.7.17.4", {"start": v(151.9, 950.4) * mm, "end": v(137.9, 950.4) * mm});
            skLineSegment(sketch, "E9.10.17.4", {"start": v(151.9, 936.4) * mm, "end": v(151.9, 950.4) * mm});
            skSolve(sketch);
        }
        {
            var Q0;
            Q0=makeQuery(id+"F9.imprint","IMPRINT",FACE,{"disambiguationData":[TD([[makeQuery(id+"F9.imprint","IMPRINT",EDGE,{"derivedFrom":sQuery(id+"F9.wireOp",EDGE,"E6.bottom")}),-1.0]])]});
            var Q1;
            Q1=makeQuery(id+"F9.imprint","IMPRINT",FACE,{"disambiguationData":[TD([[makeQuery(id+"F9.imprint","IMPRINT",EDGE,{"derivedFrom":sQuery(id+"F9.wireOp",EDGE,"E7.0.1.0")}),-1.0]])]});
            var Q2;
            Q2=makeQuery(id+"F9.imprint","IMPRINT",FACE,{"disambiguationData":[TD([[makeQuery(id+"F9.imprint","IMPRINT",EDGE,{"derivedFrom":sQuery(id+"F9.wireOp",EDGE,"E9.0.0.2")}),-1.0]])]});
            var Q3;
            Q3=makeQuery(id+"F9.imprint","IMPRINT",FACE,{"disambiguationData":[TD([[makeQuery(id+"F9.imprint","IMPRINT",EDGE,{"derivedFrom":sQuery(id+"F9.wireOp",EDGE,"E9.0.0.4")}),-1.0]])]});
            var Q4;
            Q4=makeQuery(id+"F9.imprint","IMPRINT",FACE,{"disambiguationData":[TD([[makeQuery(id+"F9.imprint","IMPRINT",EDGE,{"derivedFrom":sQuery(id+"F9.wireOp",EDGE,"E7.2.0.0")}),-1.0]])]});
            var Q5;
            Q5=makeQuery(id+"F9.imprint","IMPRINT",FACE,{"disambiguationData":[TD([[makeQuery(id+"F9.imprint","IMPRINT",EDGE,{"derivedFrom":sQuery(id+"F9.wireOp",EDGE,"E7.1.1.0")}),-1.0]])]});
            var Q6;
            Q6=makeQuery(id+"F9.imprint","IMPRINT",FACE,{"disambiguationData":[TD([[makeQuery(id+"F9.imprint","IMPRINT",EDGE,{"derivedFrom":sQuery(id+"F9.wireOp",EDGE,"E9.0.1.2")}),-1.0]])]});
            var Q7;
            Q7=makeQuery(id+"F9.imprint","IMPRINT",FACE,{"disambiguationData":[TD([[makeQuery(id+"F9.imprint","IMPRINT",EDGE,{"derivedFrom":sQuery(id+"F9.wireOp",EDGE,"E9.0.1.3")}),-1.0]])]});
            var Q8;
            Q8=makeQuery(id+"F9.imprint","IMPRINT",FACE,{"disambiguationData":[TD([[makeQuery(id+"F9.imprint","IMPRINT",EDGE,{"derivedFrom":sQuery(id+"F9.wireOp",EDGE,"E9.0.2.3")}),-1.0]])]});
            var Q9;
            Q9=makeQuery(id+"F9.imprint","IMPRINT",FACE,{"disambiguationData":[TD([[makeQuery(id+"F9.imprint","IMPRINT",EDGE,{"derivedFrom":sQuery(id+"F9.wireOp",EDGE,"E9.0.2.4")}),-1.0]])]});
            var Q10;
            Q10=makeQuery(id+"F9.imprint","IMPRINT",FACE,{"disambiguationData":[TD([[makeQuery(id+"F9.imprint","IMPRINT",EDGE,{"derivedFrom":sQuery(id+"F9.wireOp",EDGE,"E9.0.2.2")}),-1.0]])]});
            var Q11;
            Q11=makeQuery(id+"F9.imprint","IMPRINT",FACE,{"disambiguationData":[TD([[makeQuery(id+"F9.imprint","IMPRINT",EDGE,{"derivedFrom":sQuery(id+"F9.wireOp",EDGE,"E7.2.1.0")}),-1.0]])]});
            var Q12;
            Q12=makeQuery(id+"F9.imprint","IMPRINT",FACE,{"disambiguationData":[TD([[makeQuery(id+"F9.imprint","IMPRINT",EDGE,{"derivedFrom":sQuery(id+"F9.wireOp",EDGE,"E9.0.3.3")}),-1.0]])]});
            var Q13;
            Q13=makeQuery(id+"F9.imprint","IMPRINT",FACE,{"disambiguationData":[TD([[makeQuery(id+"F9.imprint","IMPRINT",EDGE,{"derivedFrom":sQuery(id+"F9.wireOp",EDGE,"E9.0.3.2")}),-1.0]])]});
            var Q14;
            Q14=makeQuery(id+"F9.imprint","IMPRINT",FACE,{"disambiguationData":[TD([[makeQuery(id+"F9.imprint","IMPRINT",EDGE,{"derivedFrom":sQuery(id+"F9.wireOp",EDGE,"E8.0.3.1")}),-1.0]])]});
            var Q15;
            Q15=makeQuery(id+"F9.imprint","IMPRINT",FACE,{"disambiguationData":[TD([[makeQuery(id+"F9.imprint","IMPRINT",EDGE,{"derivedFrom":sQuery(id+"F9.wireOp",EDGE,"E8.0.3.0")}),-1.0]])]});
            var Q16;
            Q16=makeQuery(id+"F9.imprint","IMPRINT",FACE,{"disambiguationData":[TD([[makeQuery(id+"F9.imprint","IMPRINT",EDGE,{"derivedFrom":sQuery(id+"F9.wireOp",EDGE,"E9.0.4.4")}),-1.0]])]});
            var Q17;
            Q17=makeQuery(id+"F9.imprint","IMPRINT",FACE,{"disambiguationData":[TD([[makeQuery(id+"F9.imprint","IMPRINT",EDGE,{"derivedFrom":sQuery(id+"F9.wireOp",EDGE,"E9.0.5.4")}),-1.0]])]});
            var Q18;
            Q18=makeQuery(id+"F9.imprint","IMPRINT",FACE,{"disambiguationData":[TD([[makeQuery(id+"F9.imprint","IMPRINT",EDGE,{"derivedFrom":sQuery(id+"F9.wireOp",EDGE,"E9.0.6.4")}),-1.0]])]});
            var Q19;
            Q19=makeQuery(id+"F9.imprint","IMPRINT",FACE,{"disambiguationData":[TD([[makeQuery(id+"F9.imprint","IMPRINT",EDGE,{"derivedFrom":sQuery(id+"F9.wireOp",EDGE,"E9.0.7.4")}),-1.0]])]});
            var Q20;
            Q20=makeQuery(id+"F9.imprint","IMPRINT",FACE,{"disambiguationData":[TD([[makeQuery(id+"F9.imprint","IMPRINT",EDGE,{"derivedFrom":sQuery(id+"F9.wireOp",EDGE,"E9.0.8.4")}),-1.0]])]});
            var Q21;
            Q21=makeQuery(id+"F9.imprint","IMPRINT",FACE,{"disambiguationData":[TD([[makeQuery(id+"F9.imprint","IMPRINT",EDGE,{"derivedFrom":sQuery(id+"F9.wireOp",EDGE,"E9.0.10.4")}),-1.0]])]});
            var Q22;
            Q22=makeQuery(id+"F9.imprint","IMPRINT",FACE,{"disambiguationData":[TD([[makeQuery(id+"F9.imprint","IMPRINT",EDGE,{"derivedFrom":sQuery(id+"F9.wireOp",EDGE,"E9.0.11.4")}),-1.0]])]});
            var Q23;
            Q23=makeQuery(id+"F9.imprint","IMPRINT",FACE,{"disambiguationData":[TD([[makeQuery(id+"F9.imprint","IMPRINT",EDGE,{"derivedFrom":sQuery(id+"F9.wireOp",EDGE,"E9.0.11.3")}),-1.0]])]});
            var Q24;
            Q24=makeQuery(id+"F9.imprint","IMPRINT",FACE,{"disambiguationData":[TD([[makeQuery(id+"F9.imprint","IMPRINT",EDGE,{"derivedFrom":sQuery(id+"F9.wireOp",EDGE,"E9.0.12.4")}),-1.0]])]});
            var Q25;
            Q25=makeQuery(id+"F9.imprint","IMPRINT",FACE,{"disambiguationData":[TD([[makeQuery(id+"F9.imprint","IMPRINT",EDGE,{"derivedFrom":sQuery(id+"F9.wireOp",EDGE,"E9.0.15.3")}),-1.0]])]});
            var Q26;
            Q26=makeQuery(id+"F9.imprint","IMPRINT",FACE,{"disambiguationData":[TD([[makeQuery(id+"F9.imprint","IMPRINT",EDGE,{"derivedFrom":sQuery(id+"F9.wireOp",EDGE,"E9.0.15.4")}),-1.0]])]});
            var Q27;
            Q27=makeQuery(id+"F9.imprint","IMPRINT",FACE,{"disambiguationData":[TD([[makeQuery(id+"F9.imprint","IMPRINT",EDGE,{"derivedFrom":sQuery(id+"F9.wireOp",EDGE,"E9.0.16.3")}),-1.0]])]});
            var Q28;
            Q28=makeQuery(id+"F9.imprint","IMPRINT",FACE,{"disambiguationData":[TD([[makeQuery(id+"F9.imprint","IMPRINT",EDGE,{"derivedFrom":sQuery(id+"F9.wireOp",EDGE,"E9.0.14.3")}),-1.0]])]});
            var Q29;
            Q29=makeQuery(id+"F9.imprint","IMPRINT",FACE,{"disambiguationData":[TD([[makeQuery(id+"F9.imprint","IMPRINT",EDGE,{"derivedFrom":sQuery(id+"F9.wireOp",EDGE,"E9.0.16.4")}),-1.0]])]});
            var Q30;
            Q30=makeQuery(id+"F9.imprint","IMPRINT",FACE,{"disambiguationData":[TD([[makeQuery(id+"F9.imprint","IMPRINT",EDGE,{"derivedFrom":sQuery(id+"F9.wireOp",EDGE,"E9.0.17.3")}),-1.0]])]});
            var Q31;
            Q31=makeQuery(id+"F9.imprint","IMPRINT",FACE,{"disambiguationData":[TD([[makeQuery(id+"F9.imprint","IMPRINT",EDGE,{"derivedFrom":sQuery(id+"F9.wireOp",EDGE,"E9.0.17.2")}),-1.0]])]});
            var Q32;
            Q32=makeQuery(id+"F9.imprint","IMPRINT",FACE,{"disambiguationData":[TD([[makeQuery(id+"F9.imprint","IMPRINT",EDGE,{"derivedFrom":sQuery(id+"F9.wireOp",EDGE,"E9.0.16.2")}),-1.0]])]});
            var Q33;
            Q33=makeQuery(id+"F9.imprint","IMPRINT",FACE,{"disambiguationData":[TD([[makeQuery(id+"F9.imprint","IMPRINT",EDGE,{"derivedFrom":sQuery(id+"F9.wireOp",EDGE,"E9.0.15.2")}),-1.0]])]});
            var Q34;
            Q34=makeQuery(id+"F9.imprint","IMPRINT",FACE,{"disambiguationData":[TD([[makeQuery(id+"F9.imprint","IMPRINT",EDGE,{"derivedFrom":sQuery(id+"F9.wireOp",EDGE,"E9.0.14.2")}),-1.0]])]});
            var Q35;
            Q35=makeQuery(id+"F9.imprint","IMPRINT",FACE,{"disambiguationData":[TD([[makeQuery(id+"F9.imprint","IMPRINT",EDGE,{"derivedFrom":sQuery(id+"F9.wireOp",EDGE,"E8.0.14.1")}),-1.0]])]});
            var Q36;
            Q36=makeQuery(id+"F9.imprint","IMPRINT",FACE,{"disambiguationData":[TD([[makeQuery(id+"F9.imprint","IMPRINT",EDGE,{"derivedFrom":sQuery(id+"F9.wireOp",EDGE,"E8.0.15.1")}),-1.0]])]});
            var Q37;
            Q37=makeQuery(id+"F9.imprint","IMPRINT",FACE,{"disambiguationData":[TD([[makeQuery(id+"F9.imprint","IMPRINT",EDGE,{"derivedFrom":sQuery(id+"F9.wireOp",EDGE,"E8.0.16.1")}),-1.0]])]});
            var Q38;
            Q38=makeQuery(id+"F9.imprint","IMPRINT",FACE,{"disambiguationData":[TD([[makeQuery(id+"F9.imprint","IMPRINT",EDGE,{"derivedFrom":sQuery(id+"F9.wireOp",EDGE,"E8.0.17.1")}),-1.0]])]});
            var Q39;
            Q39=makeQuery(id+"F9.imprint","IMPRINT",FACE,{"disambiguationData":[TD([[makeQuery(id+"F9.imprint","IMPRINT",EDGE,{"derivedFrom":sQuery(id+"F9.wireOp",EDGE,"E8.0.12.0")}),-1.0]])]});
            var Q40;
            Q40=makeQuery(id+"F9.imprint","IMPRINT",FACE,{"disambiguationData":[TD([[makeQuery(id+"F9.imprint","IMPRINT",EDGE,{"derivedFrom":sQuery(id+"F9.wireOp",EDGE,"E8.0.12.1")}),-1.0]])]});
            var Q41;
            Q41=makeQuery(id+"F9.imprint","IMPRINT",FACE,{"disambiguationData":[TD([[makeQuery(id+"F9.imprint","IMPRINT",EDGE,{"derivedFrom":sQuery(id+"F9.wireOp",EDGE,"E8.0.11.1")}),-1.0]])]});
            var Q42;
            Q42=makeQuery(id+"F9.imprint","IMPRINT",FACE,{"disambiguationData":[TD([[makeQuery(id+"F9.imprint","IMPRINT",EDGE,{"derivedFrom":sQuery(id+"F9.wireOp",EDGE,"E8.0.10.1")}),-1.0]])]});
            var Q43;
            Q43=makeQuery(id+"F9.imprint","IMPRINT",FACE,{"disambiguationData":[TD([[makeQuery(id+"F9.imprint","IMPRINT",EDGE,{"derivedFrom":sQuery(id+"F9.wireOp",EDGE,"E9.0.9.2")}),-1.0]])]});
            var Q44;
            Q44=makeQuery(id+"F9.imprint","IMPRINT",FACE,{"disambiguationData":[TD([[makeQuery(id+"F9.imprint","IMPRINT",EDGE,{"derivedFrom":sQuery(id+"F9.wireOp",EDGE,"E9.0.9.3")}),-1.0]])]});
            var Q45;
            Q45=makeQuery(id+"F9.imprint","IMPRINT",FACE,{"disambiguationData":[TD([[makeQuery(id+"F9.imprint","IMPRINT",EDGE,{"derivedFrom":sQuery(id+"F9.wireOp",EDGE,"E9.0.8.3")}),-1.0]])]});
            var Q46;
            Q46=makeQuery(id+"F9.imprint","IMPRINT",FACE,{"disambiguationData":[TD([[makeQuery(id+"F9.imprint","IMPRINT",EDGE,{"derivedFrom":sQuery(id+"F9.wireOp",EDGE,"E9.0.7.3")}),-1.0]])]});
            var Q47;
            Q47=makeQuery(id+"F9.imprint","IMPRINT",FACE,{"disambiguationData":[TD([[makeQuery(id+"F9.imprint","IMPRINT",EDGE,{"derivedFrom":sQuery(id+"F9.wireOp",EDGE,"E9.0.6.3")}),-1.0]])]});
            var Q48;
            Q48=makeQuery(id+"F9.imprint","IMPRINT",FACE,{"disambiguationData":[TD([[makeQuery(id+"F9.imprint","IMPRINT",EDGE,{"derivedFrom":sQuery(id+"F9.wireOp",EDGE,"E9.0.5.3")}),-1.0]])]});
            var Q49;
            Q49=makeQuery(id+"F9.imprint","IMPRINT",FACE,{"disambiguationData":[TD([[makeQuery(id+"F9.imprint","IMPRINT",EDGE,{"derivedFrom":sQuery(id+"F9.wireOp",EDGE,"E9.0.4.3")}),-1.0]])]});
            var Q50;
            Q50=makeQuery(id+"F9.imprint","IMPRINT",FACE,{"disambiguationData":[TD([[makeQuery(id+"F9.imprint","IMPRINT",EDGE,{"derivedFrom":sQuery(id+"F9.wireOp",EDGE,"E9.0.4.2")}),-1.0]])]});
            var Q51;
            Q51=makeQuery(id+"F9.imprint","IMPRINT",FACE,{"disambiguationData":[TD([[makeQuery(id+"F9.imprint","IMPRINT",EDGE,{"derivedFrom":sQuery(id+"F9.wireOp",EDGE,"E9.0.5.2")}),-1.0]])]});
            var Q52;
            Q52=makeQuery(id+"F9.imprint","IMPRINT",FACE,{"disambiguationData":[TD([[makeQuery(id+"F9.imprint","IMPRINT",EDGE,{"derivedFrom":sQuery(id+"F9.wireOp",EDGE,"E9.0.6.2")}),-1.0]])]});
            var Q53;
            Q53=makeQuery(id+"F9.imprint","IMPRINT",FACE,{"disambiguationData":[TD([[makeQuery(id+"F9.imprint","IMPRINT",EDGE,{"derivedFrom":sQuery(id+"F9.wireOp",EDGE,"E9.0.7.2")}),-1.0]])]});
            var Q54;
            Q54=makeQuery(id+"F9.imprint","IMPRINT",FACE,{"disambiguationData":[TD([[makeQuery(id+"F9.imprint","IMPRINT",EDGE,{"derivedFrom":sQuery(id+"F9.wireOp",EDGE,"E9.0.8.2")}),-1.0]])]});
            var Q55;
            Q55=makeQuery(id+"F9.imprint","IMPRINT",FACE,{"disambiguationData":[TD([[makeQuery(id+"F9.imprint","IMPRINT",EDGE,{"derivedFrom":sQuery(id+"F9.wireOp",EDGE,"E8.0.9.1")}),-1.0]])]});
            var Q56;
            Q56=makeQuery(id+"F9.imprint","IMPRINT",FACE,{"disambiguationData":[TD([[makeQuery(id+"F9.imprint","IMPRINT",EDGE,{"derivedFrom":sQuery(id+"F9.wireOp",EDGE,"E8.0.8.1")}),-1.0]])]});
            var Q57;
            Q57=makeQuery(id+"F9.imprint","IMPRINT",FACE,{"disambiguationData":[TD([[makeQuery(id+"F9.imprint","IMPRINT",EDGE,{"derivedFrom":sQuery(id+"F9.wireOp",EDGE,"E8.0.7.1")}),-1.0]])]});
            var Q58;
            Q58=makeQuery(id+"F9.imprint","IMPRINT",FACE,{"disambiguationData":[TD([[makeQuery(id+"F9.imprint","IMPRINT",EDGE,{"derivedFrom":sQuery(id+"F9.wireOp",EDGE,"E8.0.6.1")}),-1.0]])]});
            var Q59;
            Q59=makeQuery(id+"F9.imprint","IMPRINT",FACE,{"disambiguationData":[TD([[makeQuery(id+"F9.imprint","IMPRINT",EDGE,{"derivedFrom":sQuery(id+"F9.wireOp",EDGE,"E8.0.5.1")}),-1.0]])]});
            var Q60;
            Q60=makeQuery(id+"F9.imprint","IMPRINT",FACE,{"disambiguationData":[TD([[makeQuery(id+"F9.imprint","IMPRINT",EDGE,{"derivedFrom":sQuery(id+"F9.wireOp",EDGE,"E8.0.4.1")}),-1.0]])]});
            var Q61;
            Q61=makeQuery(id+"F9.imprint","IMPRINT",FACE,{"disambiguationData":[TD([[makeQuery(id+"F9.imprint","IMPRINT",EDGE,{"derivedFrom":sQuery(id+"F9.wireOp",EDGE,"E8.0.5.0")}),-1.0]])]});
            var Q62;
            Q62=makeQuery(id+"F9.imprint","IMPRINT",FACE,{"disambiguationData":[TD([[makeQuery(id+"F9.imprint","IMPRINT",EDGE,{"derivedFrom":sQuery(id+"F9.wireOp",EDGE,"E8.0.6.0")}),-1.0]])]});
            var Q63;
            Q63=makeQuery(id+"F9.imprint","IMPRINT",FACE,{"disambiguationData":[TD([[makeQuery(id+"F9.imprint","IMPRINT",EDGE,{"derivedFrom":sQuery(id+"F9.wireOp",EDGE,"E8.0.7.0")}),-1.0]])]});
            var Q64;
            Q64=makeQuery(id+"F9.imprint","IMPRINT",FACE,{"disambiguationData":[TD([[makeQuery(id+"F9.imprint","IMPRINT",EDGE,{"derivedFrom":sQuery(id+"F9.wireOp",EDGE,"E8.0.10.0")}),-1.0]])]});
            var Q65;
            Q65=makeQuery(id+"F9.imprint","IMPRINT",FACE,{"disambiguationData":[TD([[makeQuery(id+"F9.imprint","IMPRINT",EDGE,{"derivedFrom":sQuery(id+"F9.wireOp",EDGE,"E8.0.11.0")}),-1.0]])]});
            var Q66;
            Q66=makeQuery(id+"F9.imprint","IMPRINT",FACE,{"disambiguationData":[TD([[makeQuery(id+"F9.imprint","IMPRINT",EDGE,{"derivedFrom":sQuery(id+"F9.wireOp",EDGE,"E8.0.8.0")}),-1.0]])]});
            extrude(context, id + "F10", {"entities" : qUnion([Q0, Q1, Q2, Q3, Q4, Q5, Q6, Q7, Q8, Q9, Q10, Q11, Q12, Q13, Q14, Q15, Q16, Q17, Q18, Q19, Q20, Q21, Q22, Q23, Q24, Q25, Q26, Q27, Q28, Q29, Q30, Q31, Q32, Q33, Q34, Q35, Q36, Q37, Q38, Q39, Q40, Q41, Q42, Q43, Q44, Q45, Q46, Q47, Q48, Q49, Q50, Q51, Q52, Q53, Q54, Q55, Q56, Q57, Q58, Q59, Q60, Q61, Q62, Q63, Q64, Q65, Q66]), "operationType" : NewBodyOperationType.ADD, "depth" : 4 * mm});
        }
        {
            var Q0;
            Q0=makeQuery(id+"F10.opExtrude","SWEPT_FACE",FACE,{"disambiguationData":[OSD([sQuery(id+"F9.wireOp",EDGE,"E9.10.4.4")])]});
            var Q1;
            Q1=makeQuery(id+"F10.opExtrude","SWEPT_FACE",FACE,{"disambiguationData":[OSD([sQuery(id+"F9.wireOp",EDGE,"E9.10.5.4")])]});
            var Q2;
            Q2=makeQuery(id+"F10.opExtrude","SWEPT_FACE",FACE,{"disambiguationData":[OSD([sQuery(id+"F9.wireOp",EDGE,"E9.10.6.4")])]});
            var Q3;
            Q3=makeQuery(id+"F10.opExtrude","SWEPT_FACE",FACE,{"disambiguationData":[OSD([sQuery(id+"F9.wireOp",EDGE,"E9.10.7.4")])]});
            var Q4;
            Q4=makeQuery(id+"F10.opExtrude","SWEPT_FACE",FACE,{"disambiguationData":[OSD([sQuery(id+"F9.wireOp",EDGE,"E9.10.8.3")])]});
            extrude(context, id + "F11", {"entities" : qUnion([Q0, Q1, Q2, Q3, Q4]), "operationType" : NewBodyOperationType.ADD, "endBound" : BoundingType.UP_TO_NEXT, "depth" : 25 * mm});
        }
        {
            var Q0;
            Q0=makeQuery(id+"F10.opExtrude","SWEPT_FACE",FACE,{"disambiguationData":[OSD([sQuery(id+"F9.wireOp",EDGE,"E9.4.9.2")])]});
            extrude(context, id + "F12", {"entities" : qUnion([Q0]), "operationType" : NewBodyOperationType.ADD, "endBound" : BoundingType.UP_TO_NEXT, "depth" : 25 * mm});
        }
        {
            var Q0;
            Q0=makeQuery(id+"F10.opExtrude","CAP_FACE",FACE,{"disambiguationData":[OSD([sQuery(id+"F9.wireOp",EDGE,"E6.bottom"),sQuery(id+"F9.wireOp",EDGE,"E6.top"),sQuery(id+"F9.wireOp",EDGE,"E6.left"),sQuery(id+"F9.wireOp",EDGE,"E6.right")])],"isStart":false});
            var Q1;
            Q1=makeQuery(id+"F10.opExtrude","CAP_FACE",FACE,{"disambiguationData":[OSD([sQuery(id+"F9.wireOp",EDGE,"E7.0.1.0"),sQuery(id+"F9.wireOp",EDGE,"E7.0.1.2"),sQuery(id+"F9.wireOp",EDGE,"E7.0.1.3"),sQuery(id+"F9.wireOp",EDGE,"E7.0.1.4")])],"isStart":false});
            var Q2;
            Q2=makeQuery(id+"F10.opExtrude","CAP_FACE",FACE,{"disambiguationData":[OSD([sQuery(id+"F9.wireOp",EDGE,"E9.0.0.2"),sQuery(id+"F9.wireOp",EDGE,"E9.4.0.2"),sQuery(id+"F9.wireOp",EDGE,"E9.7.0.2"),sQuery(id+"F9.wireOp",EDGE,"E9.10.0.2")])],"isStart":false});
            var Q3;
            Q3=makeQuery(id+"F10.opExtrude","CAP_FACE",FACE,{"disambiguationData":[OSD([sQuery(id+"F9.wireOp",EDGE,"E9.0.0.4"),sQuery(id+"F9.wireOp",EDGE,"E9.4.0.4"),sQuery(id+"F9.wireOp",EDGE,"E9.7.0.4"),sQuery(id+"F9.wireOp",EDGE,"E9.10.0.4")])],"isStart":false});
            var Q4;
            Q4=makeQuery(id+"F10.opExtrude","CAP_FACE",FACE,{"disambiguationData":[OSD([sQuery(id+"F9.wireOp",EDGE,"E9.0.2.4"),sQuery(id+"F9.wireOp",EDGE,"E9.4.2.4"),sQuery(id+"F9.wireOp",EDGE,"E9.7.2.4"),sQuery(id+"F9.wireOp",EDGE,"E9.10.2.4")])],"isStart":false});
            var Q5;
            Q5=makeQuery(id+"F10.opExtrude","CAP_FACE",FACE,{"disambiguationData":[OSD([sQuery(id+"F9.wireOp",EDGE,"E9.0.1.3"),sQuery(id+"F9.wireOp",EDGE,"E9.4.1.3"),sQuery(id+"F9.wireOp",EDGE,"E9.7.1.3"),sQuery(id+"F9.wireOp",EDGE,"E9.10.1.3")])],"isStart":false});
            var Q6;
            Q6=makeQuery(id+"F10.opExtrude","CAP_FACE",FACE,{"disambiguationData":[OSD([sQuery(id+"F9.wireOp",EDGE,"E9.0.1.2"),sQuery(id+"F9.wireOp",EDGE,"E9.4.1.2"),sQuery(id+"F9.wireOp",EDGE,"E9.7.1.2"),sQuery(id+"F9.wireOp",EDGE,"E9.10.1.2")])],"isStart":false});
            var Q7;
            Q7=makeQuery(id+"F10.opExtrude","CAP_FACE",FACE,{"disambiguationData":[OSD([sQuery(id+"F9.wireOp",EDGE,"E7.1.1.0"),sQuery(id+"F9.wireOp",EDGE,"E7.1.1.2"),sQuery(id+"F9.wireOp",EDGE,"E7.1.1.3"),sQuery(id+"F9.wireOp",EDGE,"E7.1.1.4")])],"isStart":false});
            var Q8;
            Q8=makeQuery(id+"F10.opExtrude","CAP_FACE",FACE,{"disambiguationData":[OSD([sQuery(id+"F9.wireOp",EDGE,"E7.2.0.0"),sQuery(id+"F9.wireOp",EDGE,"E7.2.0.2"),sQuery(id+"F9.wireOp",EDGE,"E7.2.0.3"),sQuery(id+"F9.wireOp",EDGE,"E7.2.0.4")])],"isStart":false});
            var Q9;
            Q9=makeQuery(id+"F10.opExtrude","CAP_FACE",FACE,{"disambiguationData":[OSD([sQuery(id+"F9.wireOp",EDGE,"E8.0.3.0"),sQuery(id+"F9.wireOp",EDGE,"E8.4.3.0"),sQuery(id+"F9.wireOp",EDGE,"E8.7.3.0"),sQuery(id+"F9.wireOp",EDGE,"E8.10.3.0")])],"isStart":false});
            var Q10;
            Q10=makeQuery(id+"F10.opExtrude","CAP_FACE",FACE,{"disambiguationData":[OSD([sQuery(id+"F9.wireOp",EDGE,"E7.2.1.0"),sQuery(id+"F9.wireOp",EDGE,"E7.2.1.2"),sQuery(id+"F9.wireOp",EDGE,"E7.2.1.3"),sQuery(id+"F9.wireOp",EDGE,"E7.2.1.4")])],"isStart":false});
            var Q11;
            Q11=makeQuery(id+"F10.opExtrude","CAP_FACE",FACE,{"disambiguationData":[OSD([sQuery(id+"F9.wireOp",EDGE,"E9.0.2.2"),sQuery(id+"F9.wireOp",EDGE,"E9.4.2.2"),sQuery(id+"F9.wireOp",EDGE,"E9.7.2.2"),sQuery(id+"F9.wireOp",EDGE,"E9.10.2.2")])],"isStart":false});
            var Q12;
            Q12=makeQuery(id+"F10.opExtrude","CAP_FACE",FACE,{"disambiguationData":[OSD([sQuery(id+"F9.wireOp",EDGE,"E9.0.2.3"),sQuery(id+"F9.wireOp",EDGE,"E9.4.2.3"),sQuery(id+"F9.wireOp",EDGE,"E9.7.2.3"),sQuery(id+"F9.wireOp",EDGE,"E9.10.2.3")])],"isStart":false});
            var Q13;
            Q13=makeQuery(id+"F10.opExtrude","CAP_FACE",FACE,{"disambiguationData":[OSD([sQuery(id+"F9.wireOp",EDGE,"E9.0.3.3"),sQuery(id+"F9.wireOp",EDGE,"E9.4.3.3"),sQuery(id+"F9.wireOp",EDGE,"E9.7.3.3"),sQuery(id+"F9.wireOp",EDGE,"E9.10.3.3")])],"isStart":false});
            var Q14;
            Q14=makeQuery(id+"F10.opExtrude","CAP_FACE",FACE,{"disambiguationData":[OSD([sQuery(id+"F9.wireOp",EDGE,"E9.0.3.2"),sQuery(id+"F9.wireOp",EDGE,"E9.4.3.2"),sQuery(id+"F9.wireOp",EDGE,"E9.7.3.2"),sQuery(id+"F9.wireOp",EDGE,"E9.10.3.2")])],"isStart":false});
            var Q15;
            Q15=makeQuery(id+"F10.opExtrude","CAP_FACE",FACE,{"disambiguationData":[OSD([sQuery(id+"F9.wireOp",EDGE,"E8.0.3.1"),sQuery(id+"F9.wireOp",EDGE,"E8.4.3.1"),sQuery(id+"F9.wireOp",EDGE,"E8.7.3.1"),sQuery(id+"F9.wireOp",EDGE,"E8.10.3.1")])],"isStart":false});
            var Q16;
            Q16=makeQuery(id+"F10.opExtrude","CAP_FACE",FACE,{"disambiguationData":[OSD([sQuery(id+"F9.wireOp",EDGE,"E8.0.4.1"),sQuery(id+"F9.wireOp",EDGE,"E8.4.4.1"),sQuery(id+"F9.wireOp",EDGE,"E8.7.4.1"),sQuery(id+"F9.wireOp",EDGE,"E8.10.4.1")])],"isStart":false});
            var Q17;
            Q17=makeQuery(id+"F10.opExtrude","CAP_FACE",FACE,{"disambiguationData":[OSD([sQuery(id+"F9.wireOp",EDGE,"E9.0.4.2"),sQuery(id+"F9.wireOp",EDGE,"E9.4.4.2"),sQuery(id+"F9.wireOp",EDGE,"E9.7.4.2"),sQuery(id+"F9.wireOp",EDGE,"E9.10.4.2")])],"isStart":false});
            var Q18;
            Q18=makeQuery(id+"F10.opExtrude","CAP_FACE",FACE,{"disambiguationData":[OSD([sQuery(id+"F9.wireOp",EDGE,"E9.0.4.3"),sQuery(id+"F9.wireOp",EDGE,"E9.4.4.3"),sQuery(id+"F9.wireOp",EDGE,"E9.7.4.3"),sQuery(id+"F9.wireOp",EDGE,"E9.10.4.3")])],"isStart":false});
            var Q19;
            Q19=makeQuery(id+"F10.opExtrude","CAP_FACE",FACE,{"disambiguationData":[OSD([sQuery(id+"F9.wireOp",EDGE,"E9.0.5.3"),sQuery(id+"F9.wireOp",EDGE,"E9.4.5.3"),sQuery(id+"F9.wireOp",EDGE,"E9.7.5.3"),sQuery(id+"F9.wireOp",EDGE,"E9.10.5.3")])],"isStart":false});
            var Q20;
            Q20=makeQuery(id+"F10.opExtrude","CAP_FACE",FACE,{"disambiguationData":[OSD([sQuery(id+"F9.wireOp",EDGE,"E9.0.5.2"),sQuery(id+"F9.wireOp",EDGE,"E9.4.5.2"),sQuery(id+"F9.wireOp",EDGE,"E9.7.5.2"),sQuery(id+"F9.wireOp",EDGE,"E9.10.5.2")])],"isStart":false});
            var Q21;
            Q21=makeQuery(id+"F10.opExtrude","CAP_FACE",FACE,{"disambiguationData":[OSD([sQuery(id+"F9.wireOp",EDGE,"E8.0.5.1"),sQuery(id+"F9.wireOp",EDGE,"E8.4.5.1"),sQuery(id+"F9.wireOp",EDGE,"E8.7.5.1"),sQuery(id+"F9.wireOp",EDGE,"E8.10.5.1")])],"isStart":false});
            var Q22;
            Q22=makeQuery(id+"F10.opExtrude","CAP_FACE",FACE,{"disambiguationData":[OSD([sQuery(id+"F9.wireOp",EDGE,"E8.0.5.0"),sQuery(id+"F9.wireOp",EDGE,"E8.4.5.0"),sQuery(id+"F9.wireOp",EDGE,"E8.7.5.0"),sQuery(id+"F9.wireOp",EDGE,"E8.10.5.0")])],"isStart":false});
            var Q23;
            {var subQ0=sQuery(id+"F9.wireOp",EDGE,"E9.10.7.4");var subQ1=sQuery(id+"F9.wireOp",EDGE,"E9.10.6.4");var subQ2=sQuery(id+"F9.wireOp",EDGE,"E9.10.5.4");var subQ3=sQuery(id+"F9.wireOp",EDGE,"E9.10.4.4");Q23=makeQuery(id+"F11.boolean.opBoolean","MERGE",FACE,{"derivedFrom":[makeQuery(id+"F10.opExtrude","CAP_FACE",FACE,{"disambiguationData":[OSD([sQuery(id+"F9.wireOp",EDGE,"E9.0.4.4"),sQuery(id+"F9.wireOp",EDGE,"E9.4.4.4"),sQuery(id+"F9.wireOp",EDGE,"E9.7.4.4"),subQ3])],"isStart":false}),makeQuery(id+"F10.opExtrude","CAP_FACE",FACE,{"disambiguationData":[OSD([sQuery(id+"F9.wireOp",EDGE,"E9.0.5.4"),sQuery(id+"F9.wireOp",EDGE,"E9.4.5.4"),sQuery(id+"F9.wireOp",EDGE,"E9.7.5.4"),subQ2])],"isStart":false}),makeQuery(id+"F10.opExtrude","CAP_FACE",FACE,{"disambiguationData":[OSD([sQuery(id+"F9.wireOp",EDGE,"E9.0.6.4"),sQuery(id+"F9.wireOp",EDGE,"E9.4.6.4"),sQuery(id+"F9.wireOp",EDGE,"E9.7.6.4"),subQ1])],"isStart":false}),makeQuery(id+"F10.opExtrude","CAP_FACE",FACE,{"disambiguationData":[OSD([sQuery(id+"F9.wireOp",EDGE,"E9.0.7.4"),sQuery(id+"F9.wireOp",EDGE,"E9.4.7.4"),sQuery(id+"F9.wireOp",EDGE,"E9.7.7.4"),subQ0])],"isStart":false}),makeQuery(id+"F10.opExtrude","CAP_FACE",FACE,{"disambiguationData":[OSD([sQuery(id+"F9.wireOp",EDGE,"E9.0.8.4"),sQuery(id+"F9.wireOp",EDGE,"E9.4.8.4"),sQuery(id+"F9.wireOp",EDGE,"E9.7.8.4"),sQuery(id+"F9.wireOp",EDGE,"E9.10.8.4")])],"isStart":false}),makeQuery(id+"F11.opExtrude","SWEPT_FACE",FACE,{"disambiguationData":[OSD([subQ3]),TDD([makeQuery(id+"F10.opExtrude","CAP_EDGE",EDGE,{"disambiguationData":[OSD([subQ3])],"isStart":false})])]}),makeQuery(id+"F11.opExtrude","SWEPT_FACE",FACE,{"disambiguationData":[OSD([subQ2]),TDD([makeQuery(id+"F10.opExtrude","CAP_EDGE",EDGE,{"disambiguationData":[OSD([subQ2])],"isStart":false})])]}),makeQuery(id+"F11.opExtrude","SWEPT_FACE",FACE,{"disambiguationData":[OSD([subQ1]),TDD([makeQuery(id+"F10.opExtrude","CAP_EDGE",EDGE,{"disambiguationData":[OSD([subQ1])],"isStart":false})])]}),makeQuery(id+"F11.opExtrude","SWEPT_FACE",FACE,{"disambiguationData":[OSD([subQ0]),TDD([makeQuery(id+"F10.opExtrude","CAP_EDGE",EDGE,{"disambiguationData":[OSD([subQ0])],"isStart":false})])]})]});}
            var Q24;
            Q24=makeQuery(id+"F10.opExtrude","CAP_FACE",FACE,{"disambiguationData":[OSD([sQuery(id+"F9.wireOp",EDGE,"E9.0.6.3"),sQuery(id+"F9.wireOp",EDGE,"E9.4.6.3"),sQuery(id+"F9.wireOp",EDGE,"E9.7.6.3"),sQuery(id+"F9.wireOp",EDGE,"E9.10.6.3")])],"isStart":false});
            var Q25;
            Q25=makeQuery(id+"F10.opExtrude","CAP_FACE",FACE,{"disambiguationData":[OSD([sQuery(id+"F9.wireOp",EDGE,"E9.0.6.2"),sQuery(id+"F9.wireOp",EDGE,"E9.4.6.2"),sQuery(id+"F9.wireOp",EDGE,"E9.7.6.2"),sQuery(id+"F9.wireOp",EDGE,"E9.10.6.2")])],"isStart":false});
            var Q26;
            Q26=makeQuery(id+"F10.opExtrude","CAP_FACE",FACE,{"disambiguationData":[OSD([sQuery(id+"F9.wireOp",EDGE,"E8.0.6.1"),sQuery(id+"F9.wireOp",EDGE,"E8.4.6.1"),sQuery(id+"F9.wireOp",EDGE,"E8.7.6.1"),sQuery(id+"F9.wireOp",EDGE,"E8.10.6.1")])],"isStart":false});
            var Q27;
            Q27=makeQuery(id+"F10.opExtrude","CAP_FACE",FACE,{"disambiguationData":[OSD([sQuery(id+"F9.wireOp",EDGE,"E8.0.6.0"),sQuery(id+"F9.wireOp",EDGE,"E8.4.6.0"),sQuery(id+"F9.wireOp",EDGE,"E8.7.6.0"),sQuery(id+"F9.wireOp",EDGE,"E8.10.6.0")])],"isStart":false});
            var Q28;
            Q28=makeQuery(id+"F10.opExtrude","CAP_FACE",FACE,{"disambiguationData":[OSD([sQuery(id+"F9.wireOp",EDGE,"E8.0.7.0"),sQuery(id+"F9.wireOp",EDGE,"E8.4.7.0"),sQuery(id+"F9.wireOp",EDGE,"E8.7.7.0"),sQuery(id+"F9.wireOp",EDGE,"E8.10.7.0")])],"isStart":false});
            var Q29;
            Q29=makeQuery(id+"F10.opExtrude","CAP_FACE",FACE,{"disambiguationData":[OSD([sQuery(id+"F9.wireOp",EDGE,"E8.0.7.1"),sQuery(id+"F9.wireOp",EDGE,"E8.4.7.1"),sQuery(id+"F9.wireOp",EDGE,"E8.7.7.1"),sQuery(id+"F9.wireOp",EDGE,"E8.10.7.1")])],"isStart":false});
            var Q30;
            Q30=makeQuery(id+"F10.opExtrude","CAP_FACE",FACE,{"disambiguationData":[OSD([sQuery(id+"F9.wireOp",EDGE,"E9.0.7.2"),sQuery(id+"F9.wireOp",EDGE,"E9.4.7.2"),sQuery(id+"F9.wireOp",EDGE,"E9.7.7.2"),sQuery(id+"F9.wireOp",EDGE,"E9.10.7.2")])],"isStart":false});
            var Q31;
            Q31=makeQuery(id+"F10.opExtrude","CAP_FACE",FACE,{"disambiguationData":[OSD([sQuery(id+"F9.wireOp",EDGE,"E9.0.7.3"),sQuery(id+"F9.wireOp",EDGE,"E9.4.7.3"),sQuery(id+"F9.wireOp",EDGE,"E9.7.7.3"),sQuery(id+"F9.wireOp",EDGE,"E9.10.7.3")])],"isStart":false});
            var Q32;
            {var subQ0=sQuery(id+"F9.wireOp",EDGE,"E9.4.9.2");var subQ1=sQuery(id+"F9.wireOp",EDGE,"E9.10.8.3");Q32=makeQuery(id+"F12.boolean.opBoolean","MERGE",FACE,{"derivedFrom":[makeQuery(id+"F10.opExtrude","CAP_FACE",FACE,{"disambiguationData":[OSD([sQuery(id+"F9.wireOp",EDGE,"E9.0.9.2"),subQ0,sQuery(id+"F9.wireOp",EDGE,"E9.7.9.2"),sQuery(id+"F9.wireOp",EDGE,"E9.10.9.2")])],"isStart":false}),makeQuery(id+"F11.boolean.opBoolean","MERGE",FACE,{"derivedFrom":[makeQuery(id+"F10.opExtrude","CAP_FACE",FACE,{"disambiguationData":[OSD([sQuery(id+"F9.wireOp",EDGE,"E9.0.8.3"),sQuery(id+"F9.wireOp",EDGE,"E9.4.8.3"),sQuery(id+"F9.wireOp",EDGE,"E9.7.8.3"),subQ1])],"isStart":false}),makeQuery(id+"F10.opExtrude","CAP_FACE",FACE,{"disambiguationData":[OSD([sQuery(id+"F9.wireOp",EDGE,"E9.0.9.3"),sQuery(id+"F9.wireOp",EDGE,"E9.4.9.3"),sQuery(id+"F9.wireOp",EDGE,"E9.7.9.3"),sQuery(id+"F9.wireOp",EDGE,"E9.10.9.3")])],"isStart":false}),makeQuery(id+"F11.opExtrude","SWEPT_FACE",FACE,{"disambiguationData":[OSD([subQ1]),TDD([makeQuery(id+"F10.opExtrude","CAP_EDGE",EDGE,{"disambiguationData":[OSD([subQ1])],"isStart":false})])]})]}),makeQuery(id+"F12.opExtrude","SWEPT_FACE",FACE,{"disambiguationData":[OSD([subQ0]),TDD([makeQuery(id+"F10.opExtrude","CAP_EDGE",EDGE,{"disambiguationData":[OSD([subQ0])],"isStart":false})])]})]});}
            var Q33;
            Q33=makeQuery(id+"F10.opExtrude","CAP_FACE",FACE,{"disambiguationData":[OSD([sQuery(id+"F9.wireOp",EDGE,"E9.0.8.2"),sQuery(id+"F9.wireOp",EDGE,"E9.4.8.2"),sQuery(id+"F9.wireOp",EDGE,"E9.7.8.2"),sQuery(id+"F9.wireOp",EDGE,"E9.10.8.2")])],"isStart":false});
            var Q34;
            Q34=makeQuery(id+"F10.opExtrude","CAP_FACE",FACE,{"disambiguationData":[OSD([sQuery(id+"F9.wireOp",EDGE,"E8.0.8.1"),sQuery(id+"F9.wireOp",EDGE,"E8.4.8.1"),sQuery(id+"F9.wireOp",EDGE,"E8.7.8.1"),sQuery(id+"F9.wireOp",EDGE,"E8.10.8.1")])],"isStart":false});
            var Q35;
            Q35=makeQuery(id+"F10.opExtrude","CAP_FACE",FACE,{"disambiguationData":[OSD([sQuery(id+"F9.wireOp",EDGE,"E8.0.8.0"),sQuery(id+"F9.wireOp",EDGE,"E8.4.8.0"),sQuery(id+"F9.wireOp",EDGE,"E8.7.8.0"),sQuery(id+"F9.wireOp",EDGE,"E8.10.8.0")])],"isStart":false});
            var Q36;
            Q36=makeQuery(id+"F10.opExtrude","CAP_FACE",FACE,{"disambiguationData":[OSD([sQuery(id+"F9.wireOp",EDGE,"E8.0.9.1"),sQuery(id+"F9.wireOp",EDGE,"E8.4.9.1"),sQuery(id+"F9.wireOp",EDGE,"E8.7.9.1"),sQuery(id+"F9.wireOp",EDGE,"E8.10.9.1")])],"isStart":false});
            var Q37;
            Q37=makeQuery(id+"F10.opExtrude","CAP_FACE",FACE,{"disambiguationData":[OSD([sQuery(id+"F9.wireOp",EDGE,"E8.0.10.1"),sQuery(id+"F9.wireOp",EDGE,"E8.4.10.1"),sQuery(id+"F9.wireOp",EDGE,"E8.7.10.1"),sQuery(id+"F9.wireOp",EDGE,"E8.10.10.1")])],"isStart":false});
            var Q38;
            Q38=makeQuery(id+"F10.opExtrude","CAP_FACE",FACE,{"disambiguationData":[OSD([sQuery(id+"F9.wireOp",EDGE,"E8.0.10.0"),sQuery(id+"F9.wireOp",EDGE,"E8.4.10.0"),sQuery(id+"F9.wireOp",EDGE,"E8.7.10.0"),sQuery(id+"F9.wireOp",EDGE,"E8.10.10.0")])],"isStart":false});
            var Q39;
            Q39=makeQuery(id+"F10.opExtrude","CAP_FACE",FACE,{"disambiguationData":[OSD([sQuery(id+"F9.wireOp",EDGE,"E8.0.11.0"),sQuery(id+"F9.wireOp",EDGE,"E8.4.11.0"),sQuery(id+"F9.wireOp",EDGE,"E8.7.11.0"),sQuery(id+"F9.wireOp",EDGE,"E8.10.11.0")])],"isStart":false});
            var Q40;
            Q40=makeQuery(id+"F10.opExtrude","CAP_FACE",FACE,{"disambiguationData":[OSD([sQuery(id+"F9.wireOp",EDGE,"E8.0.11.1"),sQuery(id+"F9.wireOp",EDGE,"E8.4.11.1"),sQuery(id+"F9.wireOp",EDGE,"E8.7.11.1"),sQuery(id+"F9.wireOp",EDGE,"E8.10.11.1")])],"isStart":false});
            var Q41;
            Q41=makeQuery(id+"F10.opExtrude","CAP_FACE",FACE,{"disambiguationData":[OSD([sQuery(id+"F9.wireOp",EDGE,"E8.0.12.1"),sQuery(id+"F9.wireOp",EDGE,"E8.4.12.1"),sQuery(id+"F9.wireOp",EDGE,"E8.7.12.1"),sQuery(id+"F9.wireOp",EDGE,"E8.10.12.1")])],"isStart":false});
            var Q42;
            Q42=makeQuery(id+"F10.opExtrude","CAP_FACE",FACE,{"disambiguationData":[OSD([sQuery(id+"F9.wireOp",EDGE,"E8.0.12.0"),sQuery(id+"F9.wireOp",EDGE,"E8.4.12.0"),sQuery(id+"F9.wireOp",EDGE,"E8.7.12.0"),sQuery(id+"F9.wireOp",EDGE,"E8.10.12.0")])],"isStart":false});
            var Q43;
            Q43=makeQuery(id+"F10.opExtrude","CAP_FACE",FACE,{"disambiguationData":[OSD([sQuery(id+"F9.wireOp",EDGE,"E9.0.11.3"),sQuery(id+"F9.wireOp",EDGE,"E9.4.11.3"),sQuery(id+"F9.wireOp",EDGE,"E9.7.11.3"),sQuery(id+"F9.wireOp",EDGE,"E9.10.11.3")])],"isStart":false});
            var Q44;
            Q44=makeQuery(id+"F10.opExtrude","CAP_FACE",FACE,{"disambiguationData":[OSD([sQuery(id+"F9.wireOp",EDGE,"E9.0.10.4"),sQuery(id+"F9.wireOp",EDGE,"E9.4.10.4"),sQuery(id+"F9.wireOp",EDGE,"E9.7.10.4"),sQuery(id+"F9.wireOp",EDGE,"E9.10.10.4")])],"isStart":false});
            var Q45;
            Q45=makeQuery(id+"F10.opExtrude","CAP_FACE",FACE,{"disambiguationData":[OSD([sQuery(id+"F9.wireOp",EDGE,"E9.0.11.4"),sQuery(id+"F9.wireOp",EDGE,"E9.4.11.4"),sQuery(id+"F9.wireOp",EDGE,"E9.7.11.4"),sQuery(id+"F9.wireOp",EDGE,"E9.10.11.4")])],"isStart":false});
            var Q46;
            Q46=makeQuery(id+"F10.opExtrude","CAP_FACE",FACE,{"disambiguationData":[OSD([sQuery(id+"F9.wireOp",EDGE,"E9.0.12.4"),sQuery(id+"F9.wireOp",EDGE,"E9.4.12.4"),sQuery(id+"F9.wireOp",EDGE,"E9.7.12.4"),sQuery(id+"F9.wireOp",EDGE,"E9.10.12.4")])],"isStart":false});
            var Q47;
            Q47=makeQuery(id+"F10.opExtrude","CAP_FACE",FACE,{"disambiguationData":[OSD([sQuery(id+"F9.wireOp",EDGE,"E8.0.14.1"),sQuery(id+"F9.wireOp",EDGE,"E8.4.14.1"),sQuery(id+"F9.wireOp",EDGE,"E8.7.14.1"),sQuery(id+"F9.wireOp",EDGE,"E8.10.14.1")])],"isStart":false});
            var Q48;
            Q48=makeQuery(id+"F10.opExtrude","CAP_FACE",FACE,{"disambiguationData":[OSD([sQuery(id+"F9.wireOp",EDGE,"E8.0.15.1"),sQuery(id+"F9.wireOp",EDGE,"E8.4.15.1"),sQuery(id+"F9.wireOp",EDGE,"E8.7.15.1"),sQuery(id+"F9.wireOp",EDGE,"E8.10.15.1")])],"isStart":false});
            var Q49;
            Q49=makeQuery(id+"F10.opExtrude","CAP_FACE",FACE,{"disambiguationData":[OSD([sQuery(id+"F9.wireOp",EDGE,"E8.0.16.1"),sQuery(id+"F9.wireOp",EDGE,"E8.4.16.1"),sQuery(id+"F9.wireOp",EDGE,"E8.7.16.1"),sQuery(id+"F9.wireOp",EDGE,"E8.10.16.1")])],"isStart":false});
            var Q50;
            Q50=makeQuery(id+"F10.opExtrude","CAP_FACE",FACE,{"disambiguationData":[OSD([sQuery(id+"F9.wireOp",EDGE,"E8.0.17.1"),sQuery(id+"F9.wireOp",EDGE,"E8.4.17.1"),sQuery(id+"F9.wireOp",EDGE,"E8.7.17.1"),sQuery(id+"F9.wireOp",EDGE,"E8.10.17.1")])],"isStart":false});
            var Q51;
            Q51=makeQuery(id+"F10.opExtrude","CAP_FACE",FACE,{"disambiguationData":[OSD([sQuery(id+"F9.wireOp",EDGE,"E9.0.14.2"),sQuery(id+"F9.wireOp",EDGE,"E9.4.14.2"),sQuery(id+"F9.wireOp",EDGE,"E9.7.14.2"),sQuery(id+"F9.wireOp",EDGE,"E9.10.14.2")])],"isStart":false});
            var Q52;
            Q52=makeQuery(id+"F10.opExtrude","CAP_FACE",FACE,{"disambiguationData":[OSD([sQuery(id+"F9.wireOp",EDGE,"E9.0.15.2"),sQuery(id+"F9.wireOp",EDGE,"E9.4.15.2"),sQuery(id+"F9.wireOp",EDGE,"E9.7.15.2"),sQuery(id+"F9.wireOp",EDGE,"E9.10.15.2")])],"isStart":false});
            var Q53;
            Q53=makeQuery(id+"F10.opExtrude","CAP_FACE",FACE,{"disambiguationData":[OSD([sQuery(id+"F9.wireOp",EDGE,"E9.0.16.2"),sQuery(id+"F9.wireOp",EDGE,"E9.4.16.2"),sQuery(id+"F9.wireOp",EDGE,"E9.7.16.2"),sQuery(id+"F9.wireOp",EDGE,"E9.10.16.2")])],"isStart":false});
            var Q54;
            Q54=makeQuery(id+"F10.opExtrude","CAP_FACE",FACE,{"disambiguationData":[OSD([sQuery(id+"F9.wireOp",EDGE,"E9.0.17.2"),sQuery(id+"F9.wireOp",EDGE,"E9.4.17.2"),sQuery(id+"F9.wireOp",EDGE,"E9.7.17.2"),sQuery(id+"F9.wireOp",EDGE,"E9.10.17.2")])],"isStart":false});
            var Q55;
            Q55=makeQuery(id+"F10.opExtrude","CAP_FACE",FACE,{"disambiguationData":[OSD([sQuery(id+"F9.wireOp",EDGE,"E9.0.14.3"),sQuery(id+"F9.wireOp",EDGE,"E9.4.14.3"),sQuery(id+"F9.wireOp",EDGE,"E9.7.14.3"),sQuery(id+"F9.wireOp",EDGE,"E9.10.14.3")])],"isStart":false});
            var Q56;
            Q56=makeQuery(id+"F10.opExtrude","CAP_FACE",FACE,{"disambiguationData":[OSD([sQuery(id+"F9.wireOp",EDGE,"E9.0.15.3"),sQuery(id+"F9.wireOp",EDGE,"E9.4.15.3"),sQuery(id+"F9.wireOp",EDGE,"E9.7.15.3"),sQuery(id+"F9.wireOp",EDGE,"E9.10.15.3")])],"isStart":false});
            var Q57;
            Q57=makeQuery(id+"F10.opExtrude","CAP_FACE",FACE,{"disambiguationData":[OSD([sQuery(id+"F9.wireOp",EDGE,"E9.0.16.3"),sQuery(id+"F9.wireOp",EDGE,"E9.4.16.3"),sQuery(id+"F9.wireOp",EDGE,"E9.7.16.3"),sQuery(id+"F9.wireOp",EDGE,"E9.10.16.3")])],"isStart":false});
            var Q58;
            Q58=makeQuery(id+"F10.opExtrude","CAP_FACE",FACE,{"disambiguationData":[OSD([sQuery(id+"F9.wireOp",EDGE,"E9.0.17.3"),sQuery(id+"F9.wireOp",EDGE,"E9.4.17.3"),sQuery(id+"F9.wireOp",EDGE,"E9.7.17.3"),sQuery(id+"F9.wireOp",EDGE,"E9.10.17.3")])],"isStart":false});
            var Q59;
            Q59=makeQuery(id+"F10.opExtrude","CAP_FACE",FACE,{"disambiguationData":[OSD([sQuery(id+"F9.wireOp",EDGE,"E9.0.15.4"),sQuery(id+"F9.wireOp",EDGE,"E9.4.15.4"),sQuery(id+"F9.wireOp",EDGE,"E9.7.15.4"),sQuery(id+"F9.wireOp",EDGE,"E9.10.15.4")])],"isStart":false});
            var Q60;
            Q60=makeQuery(id+"F10.opExtrude","CAP_FACE",FACE,{"disambiguationData":[OSD([sQuery(id+"F9.wireOp",EDGE,"E9.0.16.4"),sQuery(id+"F9.wireOp",EDGE,"E9.4.16.4"),sQuery(id+"F9.wireOp",EDGE,"E9.7.16.4"),sQuery(id+"F9.wireOp",EDGE,"E9.10.16.4")])],"isStart":false});
            extrude(context, id + "F13", {"entities" : qUnion([Q0, Q1, Q2, Q3, Q4, Q5, Q6, Q7, Q8, Q9, Q10, Q11, Q12, Q13, Q14, Q15, Q16, Q17, Q18, Q19, Q20, Q21, Q22, Q23, Q24, Q25, Q26, Q27, Q28, Q29, Q30, Q31, Q32, Q33, Q34, Q35, Q36, Q37, Q38, Q39, Q40, Q41, Q42, Q43, Q44, Q45, Q46, Q47, Q48, Q49, Q50, Q51, Q52, Q53, Q54, Q55, Q56, Q57, Q58, Q59, Q60]), "operationType" : NewBodyOperationType.ADD, "depth" : 2 * mm, "hasDraft" : true, "draftAngle" : 30 * degree, "draftPullDirection" : true});
        }
    });
